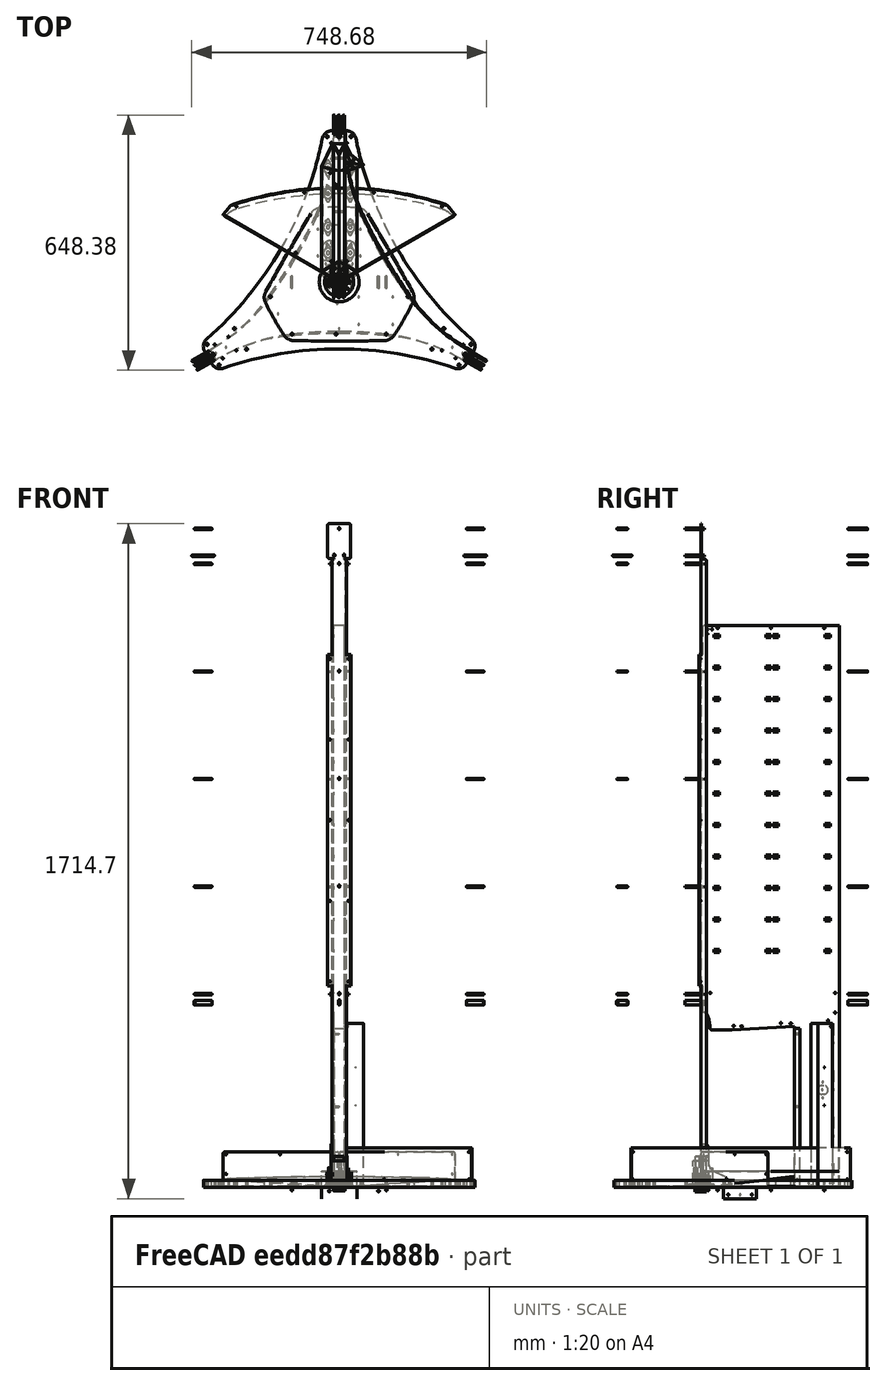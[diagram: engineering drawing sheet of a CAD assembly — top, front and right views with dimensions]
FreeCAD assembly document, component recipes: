
FREECAD ASSEMBLY — COMPONENT RECIPES ("composit_full_size3")

This assembly document has 76 components, labeled P0..P75 below (a component is one placed body or linked part). 73 of them carry a construction recipe — the FreeCAD feature program that regenerates the part from scratch, quoted from this document or its linked companion documents; the rest are supplied as boundary geometry only. No exploded tour is included for this assembly.
NOTE — document 2 of 3 of this assembly tour. The two overview renders and the header above are repeated from document 1; the component sections below continue where the previous document stopped.
COMPONENT P37 — recipe-attached ("hub2108", modeled in this document).
Construction recipe (the document's own serialized feature program — sketch geometry with constraints, then the solid features built on it; lengths are millimeters unless a unit is written):

FEATURE [PartDesign::SubShapeBinder] Binder
  BindCopyOnChange = 0
  BindMode = 0
  ClaimChildren = true
  Context = -> Body [Binder.]
  Fuse = false
  MakeFace = true
  OffsetFill = false
  OffsetIntersection = false
  OffsetJoinType = 0
  OffsetOpenResult = false
  PartialLoad = false
  Relative = true
  Support = -> [Compound001]
  _Version = 2
  expr: Support = <<part1_base>>._self
FEATURE [PartDesign::FeaturePython] BaseBend  # WARN: FeaturePython — macro-defined, semantics opaque (R4)
  BendSide = 1
  BendSketch = -> Binder
  MidPlane = false
  Reverse = false
  Suppressed = false
  length = 1428
  radius = 0.1
  thickness = 0.3
  expr: length = <<Properties>>.total_height
  expr: radius = composit_properties#<<Properties>>.bend_r
  expr: thickness = composit_properties#<<Properties>>.al_thickness
FEATURE [Sketcher::SketchObject] Sketch044
  ArcFitTolerance = 0
  AttachmentSupport = -> [YZ_Plane]
  ExternalGeometry = -> [Binder]
  FullyConstrained = false
  MakeInternals = false
  MapMode = 5
  Placement = pos=(0,0,0) rot=(0.57735,0.57735,0.57735;2.0944rad)
  expr: Constraints[16] = <<Properties>>.total_height
  expr: Constraints[23] = composit_properties#<<Properties>>.bend_r
  expr: Constraints[33] = <<Properties>>.petal_offset
  sketch-geometry (12):
    g0: LineSegment StartX=-41.6284 StartY=0 StartZ=0 EndX=4.96521 EndY=0 EndZ=0
    g1: LineSegment StartX=4.96521 StartY=0 StartZ=0 EndX=4.96521 EndY=512 EndZ=0
    g2: LineSegment StartX=4.96521 StartY=512 StartZ=0 EndX=-41.6284 EndY=512 EndZ=0
    g3: LineSegment StartX=-41.6284 StartY=512 StartZ=0 EndX=-41.6284 EndY=0 EndZ=0
    g4: LineSegment StartX=-41.6284 StartY=1428 StartZ=0 EndX=8.37158 EndY=1428 EndZ=0
    g5: LineSegment StartX=4.96521 StartY=1354 StartZ=0 EndX=-41.6284 EndY=1354 EndZ=0
    g6: LineSegment StartX=-41.6284 StartY=1354 StartZ=0 EndX=-41.6284 EndY=1428 EndZ=0
    g7: ArcOfCircle [constr] CenterX=4.96521 CenterY=0.1 CenterZ=0 NormalX=0 NormalY=0 NormalZ=1 AngleXU=0 Radius=0.1 StartAngle=3.66519 EndAngle=4.71239
    g8: LineSegment [constr] StartX=4.96521 StartY=0 StartZ=0 EndX=6.6679 EndY=0 EndZ=0
    g9: LineSegment [constr] StartX=4.87861 StartY=0.05 StartZ=0 EndX=2.02073 EndY=5 EndZ=0
    g10: LineSegment StartX=8.37158 StartY=1428 StartZ=0 EndX=4.96521 EndY=1424.59 EndZ=0
    g11: LineSegment StartX=4.96521 StartY=1424.59 StartZ=0 EndX=4.96521 EndY=1354 EndZ=0
  constraints (35):
    c: Coincident(g0,g1)
    c: Coincident(g1,g2)
    c: Coincident(g2,g3)
    c: Coincident(g3,g0)
    c: Horizontal(g0)
    c: Horizontal(g2)
    c: Vertical(g1)
    c: Vertical(g3)
    c: PointOnObject(g0,g-1)
    c: Coincident(g4,g10)
    c: Coincident(g11,g5)
    c: Coincident(g5,g6)
    c: Coincident(g6,g4)
    c: Horizontal(g4)
    c: Horizontal(g5)
    c: Vertical(g6)
    c: DistanceY(g4) = 1428
    c: DistanceY(g11,g10) = 74
    c: PointOnObject(g7,g-1)
    c: PointOnObject(g8,g-1)
    c: Tangent(g8,g7) = -1.5708
    c: Tangent(g9,g7) = 1.5708
    c: Angle(g9) = 2.0944
    c: Radius(g7) = 0.1
    c: PointOnObject(g-3,g9)
    c: DistanceY(g9) = 5
    c: PointOnObject(g7,g1)
    c: DistanceY(g1,g11) = 842
    c: Vertical(g2,g5)
    c: DistanceX(g4,g4) = 50
    c: Coincident(g10,g11)
    c: Vertical(g11)
    c: Angle(g10) = -2.35619
    c: DistanceX(g4) = 8.37158
    c: Vertical(g5,g1)
FEATURE [PartDesign::CoordinateSystem] Local_CS025  label="part1_bottom_LCS"
  AttacherType = Attacher::AttachEngine3D
  AttachmentSupport = -> [XY_Plane]
  MapMode = 5
FEATURE [PartDesign::CoordinateSystem] Local_CS026  label="part1_top_LCS"
  AttacherType = Attacher::AttachEngine3D
  AttachmentOffset = pos=(0,0,1428) rot=(0,0,1;0rad)
  AttachmentSupport = -> [XY_Plane]
  MapMode = 5
  Placement = pos=(0,0,1428) rot=(0,0,1;0rad)
  expr: .AttachmentOffset.Base.z = <<Properties>>.total_height
FEATURE [PartDesign::Boolean] Boolean001
  BaseFeature = -> BaseBend
  Group = -> [Compound016]
  Suppressed = false
  Type = 1
  UsePlacement = false
  expr: Group = <<part1_cut1>>._self
FEATURE [PartDesign::Boolean] Boolean002
  BaseFeature = -> Boolean001
  Group = -> [Compound026]
  Refine = true
  Suppressed = false
  Type = 0
  UsePlacement = false
  expr: Group = <<part1_fuse1>>._self
FEATURE [PartDesign::Pocket] Pocket025
  BaseFeature = -> Boolean002
  Direction = (-1,0,0)
  Length = 5
  Length2 = 5
  Midplane = true
  Profile = -> Sketch044
  ReferenceAxis = -> Sketch044 [N_Axis]
  Suppressed = false
  Type = 1
FEATURE [PartDesign::Boolean] Boolean005
  BaseFeature = -> Pocket025
  Group = -> [Compound024]
  Suppressed = false
  Type = 1
  UsePlacement = false
  expr: Group = <<part1_cut2>>._self
FEATURE [PartDesign::Body] Body  label="part1_material_0.30ansi"
  AllowCompound = false
  Group = -> [Binder,BaseBend,Boolean001,Boolean002,Sketch044,Pocket025,Boolean005,Local_CS025,Local_CS026]
  Origin = -> Origin
  Tip = -> Boolean005
COMPONENT P38 — same part as P37; its construction recipe is shown at P37.
COMPONENT P39 — same part as P37; its construction recipe is shown at P37.
COMPONENT P40 — recipe-attached ("top_top001", modeled in this document).
Construction recipe (the document's own serialized feature program — sketch geometry with constraints, then the solid features built on it; lengths are millimeters unless a unit is written):

FEATURE [Part::FeaturePython] Connect001  label="top_top_cut1_refined"  # WARN: FeaturePython — macro-defined, semantics opaque (R4)
  Objects = -> [Compound049]
  Refine = true
  Tolerance = 0
FEATURE [PartDesign::FeatureBase] BaseFeature
  BaseFeature = -> Hole003
  Suppressed = false
  expr: BaseFeature = <<Hole003>>._self
FEATURE [PartDesign::FeatureSubtractivePython] PDW_Sub  # link proxy (typed FeaturePython)
  BaseFeature = -> BaseFeature
  Body = Body110
  ClaimChildren = true
  EditPlacementAdjustments = false
  Enabled = 1
  LinkedObject = -> Connect001
  MeshTolerance = 0.1
  PatternBase = -> Connect001
  PatternBaseOffset = 0
  PatternBaseScale = 1
  PatternBaseScaleXYZ = (1,1,1)
  PatternOffsetCut = false
  PatternOffsetIntersection = false
  PatternOffsetJoin = 0
  PatternOffsetMode = 0
  PatternOffsetSelfIntersection = false
  PatternOperation = 0
  PatternOperationDefault = None
  PatternScaleCut = false
  PatternShapeOffset = 0
  PatternShapeScale = 1
  PatternShapeScaleXYZ = (1,1,1)
  PatternToolOffset = 0
  PatternToolScale = 1
  PatternToolScaleXYZ = (1,1,1)
  RefineMesh = true
  ShapeManagement = 0
  ShowMeshProps = false
  ShowOffsetProps = false
  ShowScaleProps = false
  ShowWarnings = true
  Suppressed = false
  TipBase = -> BaseFeature
  TipBaseOffset = 0
  TipBaseScale = 1
  TipBaseScaleXYZ = (1,1,1)
  TipOffsetCut = false
  TipOffsetIntersection = false
  TipOffsetJoin = 0
  TipOffsetMode = 0
  TipOffsetSelfIntersection = false
  TipOperation = 1
  TipOperationDefault = Cut
  TipScaleCut = false
  TipShapeOffset = 0
  TipShapeScale = 1
  TipShapeScaleXYZ = (1,1,1)
  TipTool = -> Connect001
  TipToolOffset = 0
  TipToolScale = 1
  TipToolScaleXYZ = (1,1,1)
  Type = Subtractive
  UsePatternBaseAddSubShape = false
  UsePatternToolAddSubShape = false
  UseTipBaseAddSubShape = false
  UseTipToolAddSubShape = false
  Version = 0.2023.08.13
FEATURE [PartDesign::Boolean] Boolean034
  BaseFeature = -> PDW_Sub
  Group = -> [Compound082]
  Suppressed = false
  Type = 1
  UsePlacement = false
FEATURE [PartDesign::CoordinateSystem] Local_CS031  label="dropper_fix_top_outer_LCS"
  AttacherType = Attacher::AttachEngine3D
  AttachmentSupport = -> [XY_Plane083]
  MapMode = 5
FEATURE [PartDesign::CoordinateSystem] Local_CS032  label="dropper_fix_top_inner_LCS"
  AttacherType = Attacher::AttachEngine3D
  AttachmentOffset = pos=(0,0,3) rot=(0,0,1;0rad)
  AttachmentSupport = -> [XY_Plane083]
  MapMode = 5
  Placement = pos=(0,0,3) rot=(0,0,1;0rad)
FEATURE [PartDesign::Body] Body110  label="dropper_fix_top"
  AllowCompound = false
  Group = -> [BaseFeature,PDW_Sub,Connect001,Boolean034,Local_CS031,Local_CS032]
  Origin = -> Origin083
  Tip = -> Boolean034
COMPONENT P41 — recipe-attached ("top_bottom001", modeled in this document).
Construction recipe (the document's own serialized feature program — sketch geometry with constraints, then the solid features built on it; lengths are millimeters unless a unit is written):

FEATURE [PartDesign::SubShapeBinder] Binder007
  BindCopyOnChange = 0
  BindMode = 0
  ClaimChildren = true
  Fuse = false
  MakeFace = true
  OffsetFill = false
  OffsetIntersection = false
  OffsetJoinType = 0
  OffsetOpenResult = false
  PartialLoad = false
  Relative = false
  Support = -> [Compound011]
  _Version = 2
FEATURE [PartDesign::Pad] Pad005
  Direction = (0,0,1)
  Length = 3
  Length2 = 10
  Profile = -> Binder007
  Suppressed = false
  Type = 0
FEATURE [Sketcher::SketchObject] Sketch025
  ArcFitTolerance = 0
  AttachmentSupport = -> [XY_Plane007]
  FullyConstrained = true
  MakeInternals = false
  MapMode = 5
FEATURE [PartDesign::SubShapeBinder] Binder021
  BindCopyOnChange = 0
  BindMode = 0
  ClaimChildren = true
  Fuse = false
  MakeFace = true
  OffsetFill = false
  OffsetIntersection = false
  OffsetJoinType = 0
  OffsetOpenResult = false
  PartialLoad = false
  Relative = false
  Support = -> [Compound014]
  _Version = 2
FEATURE [PartDesign::Pocket] Pocket006
  BaseFeature = -> Pad005
  Direction = (0,0,-1)
  Length = 5
  Length2 = 5
  Midplane = true
  Profile = -> Binder021
  Suppressed = false
  Type = 1
FEATURE [Sketcher::SketchObject] Sketch027
  ArcFitTolerance = 0
  AttachmentSupport = -> [XY_Plane007]
  FullyConstrained = true
  MakeInternals = false
  MapMode = 5
  sketch-geometry (1):
    g0: Circle CenterX=0 CenterY=40 CenterZ=0 NormalX=0 NormalY=0 NormalZ=1 AngleXU=0 Radius=4
  constraints (3):
    c: PointOnObject(g0,g-2)
    c: Diameter(g0) = 8
    c: DistanceY(g0) = 40
FEATURE [PartDesign::SubShapeBinder] Binder023
  BindCopyOnChange = 0
  BindMode = 0
  ClaimChildren = true
  Context = -> Body004 [Binder023.]
  Fuse = false
  MakeFace = true
  OffsetFill = false
  OffsetIntersection = false
  OffsetJoinType = 0
  OffsetOpenResult = false
  PartialLoad = false
  Relative = true
  Support = -> [Clone005]
  _Version = 2
FEATURE [Sketcher::SketchObject] Sketch028
  ArcFitTolerance = 0
  AttachmentSupport = -> [XY_Plane007]
  ExternalGeometry = -> [Binder023]
  FullyConstrained = true
  MakeInternals = false
  MapMode = 5
  expr: Constraints[9] = <<Properties>>.rivet_d
  sketch-geometry (10):
    g0: Circle CenterX=0 CenterY=59 CenterZ=0 NormalX=0 NormalY=0 NormalZ=1 AngleXU=0 Radius=1.7
    g1: Circle CenterX=0 CenterY=106.372 CenterZ=0 NormalX=0 NormalY=0 NormalZ=1 AngleXU=0 Radius=1.7
    g2: Circle CenterX=0 CenterY=181.372 CenterZ=0 NormalX=0 NormalY=0 NormalZ=1 AngleXU=0 Radius=1.7
    g3: Circle CenterX=0 CenterY=256.372 CenterZ=0 NormalX=0 NormalY=0 NormalZ=1 AngleXU=0 Radius=1.7
    g4: Circle CenterX=0 CenterY=303.743 CenterZ=0 NormalX=0 NormalY=0 NormalZ=1 AngleXU=0 Radius=1.7
    g5: LineSegment [constr] StartX=28.3 StartY=73.8716 StartZ=0 EndX=28.3 EndY=106.372 EndZ=0
    g6: LineSegment [constr] StartX=28.3 StartY=106.372 StartZ=0 EndX=28.3 EndY=138.872 EndZ=0
    g7: LineSegment [constr] StartX=28.3 StartY=138.872 StartZ=0 EndX=28.3 EndY=181.372 EndZ=0
    g8: LineSegment [constr] StartX=28.3 StartY=181.372 StartZ=0 EndX=28.3 EndY=223.872 EndZ=0
    g9: LineSegment [constr] StartX=28.3 StartY=223.872 StartZ=0 EndX=28.3 EndY=256.372 EndZ=0
  constraints (24):
    c: PointOnObject(g0,g-2)
    c: PointOnObject(g1,g-2)
    c: PointOnObject(g2,g-2)
    c: PointOnObject(g3,g-2)
    c: DistanceY(g0) = 59
    c: Equal(g0, g1-g4) x4
    c: Diameter(g0) = 3.4
    c: Coincident(g5,g-3)
    c: Vertical(g5)
    c: Coincident(g5,g6)
    c: Coincident(g6,g-4)
    c: Coincident(g6,g7)
    c: Vertical(g7)
    c: Coincident(g7,g8)
    c: Coincident(g8,g-5)
    c: Coincident(g8,g9)
    c: Vertical(g9)
    c: Equal(g5,g6)
    c: Equal(g6,g9)
    c: Equal(g7,g8)
    c: Horizontal(g2,g7)
    c: Horizontal(g1,g5)
    c: Horizontal(g3,g9)
    c: Symmetric(g0,g4,g2)
FEATURE [PartDesign::Hole] Hole003
  BaseFeature = -> Pocket006
  CustomThreadClearance = 0
  Depth = 25
  DepthType = 0
  Diameter = 3.4
  DrillForDepth = false
  DrillPoint = 1
  DrillPointAngle = 118
  HoleCutCountersinkAngle = 90
  HoleCutCustomValues = false
  HoleCutDepth = 0
  HoleCutDiameter = 6.1
  HoleCutType = 0
  ModelThread = false
  Profile = -> Sketch028
  Reversed = true
  Suppressed = false
  Tapered = false
  TaperedAngle = 90
  ThreadClass = 0
  ThreadDepth = 25
  ThreadDepthType = 0
  ThreadDirection = 0
  ThreadFit = 0
  ThreadSize = 0
  ThreadType = 0
  Threaded = false
  UseCustomThreadClearance = false
  expr: Diameter = <<Properties>>.rivet_d
FEATURE [Part::Compound] Compound048  label="top_bottom_cut1"
  Links = -> [Extrude016,Extrude017]
FEATURE [Part::FeaturePython] Connect  label="top_bottom_cut1_refined"  # WARN: FeaturePython — macro-defined, semantics opaque (R4)
  Objects = -> [Compound048]
  Refine = true
  Tolerance = 0
FEATURE [PartDesign::Boolean] Boolean033
  BaseFeature = -> Hole003
  Group = -> [Compound081]
  Suppressed = false
  Type = 1
  UsePlacement = false
FEATURE [PartDesign::FeatureSubtractivePython] PDW_Common_Sub  # link proxy (typed FeaturePython)
  BaseFeature = -> Boolean033
  Body = Body004
  ClaimChildren = true
  EditPlacementAdjustments = false
  Enabled = 1
  LinkedObject = -> Connect
  MeshTolerance = 0.1
  PatternBaseOffset = 0
  PatternBaseScale = 1
  PatternBaseScaleXYZ = (1,1,1)
  PatternOffsetCut = false
  PatternOffsetIntersection = false
  PatternOffsetJoin = 0
  PatternOffsetMode = 0
  PatternOffsetSelfIntersection = false
  PatternOperation = 3
  PatternOperationDefault = Common
  PatternScaleCut = false
  PatternShapeOffset = 0
  PatternShapeScale = 1
  PatternShapeScaleXYZ = (1,1,1)
  PatternTool = -> Compound048
  PatternToolOffset = 0
  PatternToolScale = 1
  PatternToolScaleXYZ = (1,1,1)
  Refine = true
  RefineMesh = true
  ShapeManagement = 1
  ShowMeshProps = false
  ShowOffsetProps = false
  ShowScaleProps = false
  ShowWarnings = true
  Suppressed = false
  TipBase = -> Boolean033
  TipBaseOffset = 0
  TipBaseScale = 1
  TipBaseScaleXYZ = (1,1,1)
  TipOffsetCut = false
  TipOffsetIntersection = false
  TipOffsetJoin = 0
  TipOffsetMode = 0
  TipOffsetSelfIntersection = false
  TipOperation = 1
  TipOperationDefault = Common
  TipScaleCut = false
  TipShapeOffset = 0
  TipShapeScale = 1
  TipShapeScaleXYZ = (1,1,1)
  TipTool = -> Connect
  TipToolOffset = 0
  TipToolScale = 1
  TipToolScaleXYZ = (1,1,1)
  Type = Subtractive
  UsePatternBaseAddSubShape = false
  UsePatternToolAddSubShape = false
  UseTipBaseAddSubShape = true
  UseTipToolAddSubShape = true
  Version = 0.2023.08.13
FEATURE [PartDesign::CoordinateSystem] Local_CS029  label="dropper_fix_bottom_outer_LCS"
  AttacherType = Attacher::AttachEngine3D
  AttachmentSupport = -> [XY_Plane007]
  MapMode = 5
FEATURE [PartDesign::CoordinateSystem] Local_CS030  label="dropper_fix_bottom_inner_LCS"
  AttacherType = Attacher::AttachEngine3D
  AttachmentOffset = pos=(0,0,3) rot=(0,0,1;0rad)
  AttachmentSupport = -> [XY_Plane007]
  MapMode = 5
  Placement = pos=(0,0,3) rot=(0,0,1;0rad)
FEATURE [PartDesign::Body] Body004  label="dropper_fix_bottom"
  AllowCompound = false
  Group = -> [Binder007,Pad005,Sketch025,Binder021,Pocket006,Sketch027,Sketch028,Binder023,Hole003,Boolean033,PDW_Common_Sub,Compound048,Connect,Local_CS029,Local_CS030]
  Origin = -> Origin007
  Tip = -> PDW_Common_Sub
COMPONENT P42 — recipe-attached ("cap_outer_material_0.30ansi001", modeled in this document).
Construction recipe (the document's own serialized feature program — sketch geometry with constraints, then the solid features built on it; lengths are millimeters unless a unit is written):

FEATURE [PartDesign::SubShapeBinder] Binder012
  BindCopyOnChange = 0
  BindMode = 0
  ClaimChildren = true
  Fuse = false
  MakeFace = true
  OffsetFill = false
  OffsetIntersection = false
  OffsetJoinType = 0
  OffsetOpenResult = false
  PartialLoad = false
  Placement = pos=(0,0,40) rot=(0,0,1;0rad)
  Relative = false
  Support = -> [Compound012]
  _Version = 2
FEATURE [PartDesign::SubShapeBinder] Binder013
  BindCopyOnChange = 0
  BindMode = 0
  ClaimChildren = true
  Fuse = false
  MakeFace = true
  OffsetFill = false
  OffsetIntersection = false
  OffsetJoinType = 0
  OffsetOpenResult = false
  PartialLoad = false
  Placement = pos=(0,0,40) rot=(0,0,1;0rad)
  Relative = false
  Support = -> [Compound013]
  _Version = 2
FEATURE [PartDesign::FeaturePython] BaseBend007  # WARN: FeaturePython — macro-defined, semantics opaque (R4)
  BendSide = 1
  BendSketch = -> Binder012
  MidPlane = false
  Reverse = true
  Suppressed = false
  length = 100
  radius = 0.1
  thickness = 0.3
  expr: radius = composit_properties#<<Properties>>.bend_r
  expr: thickness = composit_properties#<<Properties>>.al_thickness
FEATURE [PartDesign::FeaturePython] Bend001  # WARN: FeaturePython — macro-defined, semantics opaque (R4)
  AutoMiter = false
  BaseFeature = -> BaseBend007
  BendType = 0
  LengthList = [47]
  LengthSpec = 1
  NonperforationMaxLength = 5
  Perforate = false
  PerforationAngle = 0
  PerforationInitialLength = 5
  PerforationMaxLength = 5
  ReliefFactor = 0.7
  Suppressed = false
  UseReliefFactor = false
  angle = 90
  baseObject = -> BaseBend007 [Edge14,Edge30,Edge46,Edge62,Edge70,Edge86,Edge102,Edge116]
  bendAList = [90]
  extend1 = 0
  extend2 = 0
  gap1 = 0
  gap2 = 0
  invert = false
  kfactor = 0.5
  length = 47
  maxExtendDist = 5
  minGap = 0.1
  minReliefGap = 1
  miterangle1 = 0
  miterangle2 = 0
  offset = 0
  radius = 0.1
  reliefType = 0
  reliefd = 1
  reliefw = 0.8
  sketchflip = false
  sketchinvert = false
  unfold = false
  expr: radius = BaseBend007.radius
FEATURE [PartDesign::Pocket] Pocket002
  BaseFeature = -> Bend001
  Direction = (0,0,-1)
  Length = 5
  Length2 = 5
  Profile = -> Binder013 [Face1]
  Refine = true
  Reversed = true
  Suppressed = false
  Type = 1
FEATURE [PartDesign::SubShapeBinder] Binder014
  BindCopyOnChange = 0
  BindMode = 0
  ClaimChildren = true
  Context = -> Link012 [Binder014.]
  Fuse = false
  MakeFace = true
  OffsetFill = false
  OffsetIntersection = false
  OffsetJoinType = 0
  OffsetOpenResult = false
  PartialLoad = false
  Relative = true
  Support = -> [Sketch019]
  _Version = 2
FEATURE [Sketcher::SketchObject] Sketch020
  ArcFitTolerance = 0
  AttachmentSupport = -> [XY_Plane005]
  FullyConstrained = true
  MakeInternals = false
  MapMode = 5
  expr: Constraints[10] = composit_properties#<<Properties>>.bend_r + composit_properties#<<Properties>>.al_thickness
  sketch-geometry (5):
    g0: ArcOfCircle CenterX=0 CenterY=0.46188 CenterZ=0 NormalX=0 NormalY=0 NormalZ=1 AngleXU=0 Radius=5 StartAngle=0.523599 EndAngle=2.61799
    g1: LineSegment StartX=0 StartY=0 StartZ=0 EndX=4.53013 EndY=2.61547 EndZ=0
    g2: LineSegment StartX=4.53013 StartY=2.61547 StartZ=0 EndX=4.33013 EndY=2.96188 EndZ=0
    g3: LineSegment StartX=0 StartY=0 StartZ=0 EndX=-4.53013 EndY=2.61547 EndZ=0
    g4: LineSegment StartX=-4.53013 StartY=2.61547 StartZ=0 EndX=-4.33013 EndY=2.96188 EndZ=0
  constraints (13):
    c: PointOnObject(g0,g-2)
    c: Coincident(g1,g-1)
    c: Coincident(g2,g1)
    c: Coincident(g3,g1)
    c: Coincident(g4,g3)
    c: Perpendicular(g3,g4)
    c: Perpendicular(g1,g2)
    c: Tangent(g2,g0) = -1.5708
    c: Tangent(g4,g0) = 1.5708
    c: Equal(g4,g2)
    c: Distance(g2) = 0.4
    c: Diameter(g0) = 10
    c: Angle(g1,g3) = 2.0944
FEATURE [PartDesign::SubShapeBinder] Binder015
  BindCopyOnChange = 0
  BindMode = 0
  ClaimChildren = false
  Context = -> Link012 [Binder015.]
  Fuse = false
  MakeFace = true
  OffsetFill = false
  OffsetIntersection = false
  OffsetJoinType = 0
  OffsetOpenResult = false
  PartialLoad = false
  Relative = true
  Support = -> [Sketch002]
  _Version = 2
  expr: Support = <<dropper_fix_sketch>>._self
FEATURE [Sketcher::SketchObject] Sketch022  label="cap_outer_shape"
  ArcFitTolerance = 0
  AttachmentSupport = -> [YZ_Plane005]
  ExternalGeometry = -> [Binder012]
  FullyConstrained = true
  MakeInternals = false
  MapMode = 5
  Placement = pos=(0,0,0) rot=(0.57735,0.57735,0.57735;2.0944rad)
  expr: Constraints[11] = composit_properties#<<Properties>>.bend_r + composit_properties#<<Properties>>.al_thickness
  expr: Constraints[9] = composit_properties#<<Properties>>.bend_r + composit_properties#<<Properties>>.al_thickness + 0.01 mm
  sketch-geometry (5):
    g0: LineSegment StartX=351.882 StartY=40.41 StartZ=0 EndX=0 EndY=40.41 EndZ=0
    g1: LineSegment StartX=0 StartY=40.41 StartZ=0 EndX=0 EndY=0 EndZ=0
    g2: LineSegment StartX=0 StartY=0 StartZ=0 EndX=351.882 EndY=0 EndZ=0
    g3: LineSegment StartX=351.882 StartY=0 StartZ=0 EndX=351.882 EndY=40.41 EndZ=0
    g4: GeomPoint [constr] X=351.872 Y=40.4 Z=0
  constraints (14):
    c: Coincident(g0,g1)
    c: Coincident(g1,g2)
    c: Coincident(g2,g3)
    c: Coincident(g3,g0)
    c: Horizontal(g0)
    c: Horizontal(g2)
    c: Vertical(g1)
    c: Vertical(g3)
    c: Coincident(g1,g-1)
    c: DistanceY(g-3,g0) = 0.41
    c: DistanceX(g-3,g0) = 0.01
    c: DistanceY(g-3,g4) = 0.4
    c: Vertical(g-3,g4)
    c: DistanceY(g4) = 40.4  'height'
FEATURE [Part::FeaturePython] WireFilter002  # WARN: FeaturePython — macro-defined, semantics opaque (R4)
  AttacherType = Attacher::AttachEngine3D
  ClaimChildren = true
  ColorKeyCount = 8
  Colorize = true
  FaceMaker = 5
  FixNormal = false
  FollowSource = true
  InvertedFaceScale = 5
  MaxWires = 25
  Normal = (1,0,0)
  OffsetFill = false
  OffsetIntersection = false
  OffsetJoin = 0
  OffsetOpenResult = false
  Scale = (1,1,1)
  SelectEdges = false
  Source = -> Sketch022
  UniformScale = 1
  UseDefault = false
  UseSelected = true
  UseSelectedEdges = false
  Version = 0.2022.02.09
  WireOrder = [1]
FEATURE [PartDesign::SubShapeBinder] Binder132
  BindCopyOnChange = 0
  BindMode = 0
  ClaimChildren = true
  Fuse = false
  MakeFace = true
  OffsetFill = false
  OffsetIntersection = false
  OffsetJoinType = 0
  OffsetOpenResult = false
  PartialLoad = false
  Relative = false
  Support = -> [Sketch017]
  _Version = 2
FEATURE [PartDesign::Pocket] Pocket125
  BaseFeature = -> Pocket002
  Direction = (0,0,-1)
  Length = 5
  Length2 = 5
  Midplane = true
  Profile = -> Binder014
  Suppressed = false
  Type = 1
FEATURE [PartDesign::Pocket] Pocket003
  BaseFeature = -> Pocket125
  Direction = (0,0,-1)
  Length = 5
  Length2 = 5
  Midplane = true
  Profile = -> Sketch020
  ReferenceAxis = -> Sketch020 [N_Axis]
  Suppressed = false
  Type = 1
FEATURE [PartDesign::Mirrored] Mirrored
  BaseFeature = -> Pocket003
  MirrorPlane = -> YZ_Plane005
  Suppressed = false
  TransformMode = 0
FEATURE [PartDesign::Pocket] Pocket005
  BaseFeature = -> Mirrored
  Direction = (-1,0,0)
  Length = 5
  Length2 = 5
  Midplane = true
  Profile = -> WireFilter002
  Suppressed = false
  Type = 1
FEATURE [PartDesign::Boolean] Boolean032
  BaseFeature = -> Pocket005
  Group = -> [Compound080]
  Suppressed = false
  Type = 1
  UsePlacement = false
FEATURE [PartDesign::Body] Body002  label="cap_outer_material_0.30ansi"
  AllowCompound = false
  Group = -> [Binder012,Binder013,BaseBend007,Bend001,Pocket002,Binder014,Sketch020,Pocket125,Pocket003,Binder015,Mirrored,Sketch022,WireFilter002,Pocket005,Binder132,Boolean032]
  Origin = -> Origin005
  Tip = -> Boolean032
COMPONENT P43 — recipe-attached ("cap_inner2_material_0.30ansi001", modeled in this document).
Construction recipe (the document's own serialized feature program — sketch geometry with constraints, then the solid features built on it; lengths are millimeters unless a unit is written):

FEATURE [PartDesign::SubShapeBinder] Binder018
  BindCopyOnChange = 0
  BindMode = 0
  ClaimChildren = false
  Fuse = false
  MakeFace = true
  OffsetFill = false
  OffsetIntersection = false
  OffsetJoinType = 0
  OffsetOpenResult = false
  PartialLoad = false
  Relative = false
  Support = -> [Body002[BaseBend007.Binder012.Compound012.Part__Mirroring006.Sketch016.]]
  _Version = 2
FEATURE [PartDesign::SubShapeBinder] Binder019
  BindCopyOnChange = 0
  BindMode = 0
  ClaimChildren = false
  Fuse = false
  MakeFace = false
  OffsetFill = false
  OffsetIntersection = false
  OffsetJoinType = 0
  OffsetOpenResult = false
  PartialLoad = false
  Relative = false
  Support = -> [Sketch019]
  _Version = 2
FEATURE [Sketcher::SketchObject] Sketch024
  ArcFitTolerance = 0
  AttachmentSupport = -> [XY_Plane023]
  ExternalGeometry = -> [Binder019,Binder018]
  FullyConstrained = true
  MakeInternals = false
  MapMode = 5
  expr: Constraints[10] = composit_properties#<<Properties>>.thickness + composit_properties#<<Properties>>.al_thickness + composit_properties#<<Properties>>.bend_r
  sketch-geometry (5):
    g0: LineSegment StartX=-41.7 StartY=272.288 StartZ=0 EndX=-41.7 EndY=289.736 EndZ=0
    g1: LineSegment StartX=-41.7 StartY=289.736 StartZ=0 EndX=41.7 EndY=289.736 EndZ=0
    g2: LineSegment StartX=41.7 StartY=289.736 StartZ=0 EndX=41.7 EndY=272.288 EndZ=0
    g3: LineSegment StartX=41.7 StartY=272.288 StartZ=0 EndX=-41.7 EndY=272.288 EndZ=0
    g4: GeomPoint [constr] X=0 Y=281.012 Z=0
  constraints (13):
    c: Coincident(g0,g1)
    c: Coincident(g1,g2)
    c: Coincident(g2,g3)
    c: Coincident(g3,g0)
    c: Horizontal(g1)
    c: Horizontal(g3)
    c: Vertical(g0)
    c: Vertical(g2)
    c: Symmetric(g1,g0,g4)
    c: PointOnObject(g4,g-2)
    c: DistanceX(g1,g-4) = 3.4
    c: DistanceY(g2,g-3) = 5
    c: DistanceY(g1,g-4) = 3
FEATURE [PartDesign::FeaturePython] BaseBend008  # WARN: FeaturePython — macro-defined, semantics opaque (R4)
  BendSide = 0
  BendSketch = -> Sketch024
  MidPlane = false
  Reverse = false
  Suppressed = false
  length = 100
  radius = 0.1
  thickness = 0.3
  expr: radius = composit_properties#<<Properties>>.bend_r
  expr: thickness = composit_properties#<<Properties>>.al_thickness
FEATURE [Sketcher::SketchObject] Sketch217
  ArcFitTolerance = 0
  AttachmentSupport = -> [XY_Plane023]
  ExternalGeometry = -> [Sketch024,Binder018]
  FullyConstrained = true
  MakeInternals = false
  MapMode = 5
  sketch-geometry (6):
    g0: LineSegment StartX=41.7 StartY=289.736 StartZ=0 EndX=14.25 EndY=348.472 EndZ=0
    g1: LineSegment StartX=0 StartY=348.472 StartZ=0 EndX=14.25 EndY=348.472 EndZ=0
    g2: LineSegment [constr] StartX=14.25 StartY=351.872 StartZ=0 EndX=14.25 EndY=348.472 EndZ=0
    g3: LineSegment [constr] StartX=14.25 StartY=348.472 StartZ=0 EndX=17.3302 EndY=349.911 EndZ=0
    g4: LineSegment StartX=0 StartY=348.472 StartZ=0 EndX=0 EndY=289.736 EndZ=0
    g5: LineSegment StartX=0 StartY=289.736 StartZ=0 EndX=41.7 EndY=289.736 EndZ=0
  constraints (17):
    c: Coincident(g0,g-3)
    c: PointOnObject(g1,g-2)
    c: Coincident(g1,g0)
    c: Horizontal(g1)
    c: Coincident(g2,g0)
    c: Coincident(g2,g3)
    c: PointOnObject(g3,g-4)
    c: Perpendicular(g0,g3)
    c: Perpendicular(g1,g2)
    c: Equal(g3,g2)
    c: DistanceY(g2,g2) = 3.4
    c: Horizontal(g2,g-4)
    c: Coincident(g4,g1)
    c: PointOnObject(g4,g-3)
    c: Vertical(g4)
    c: Coincident(g5,g4)
    c: Coincident(g5,g0)
FEATURE [PartDesign::Pad] Pad033
  BaseFeature = -> BaseBend008
  Direction = (0,0,1)
  Length = 0.3
  Length2 = 10
  Profile = -> Sketch217
  ReferenceAxis = -> Sketch217 [N_Axis]
  Suppressed = false
  Type = 0
FEATURE [PartDesign::Mirrored] Mirrored016
  BaseFeature = -> Pad033
  MirrorPlane = -> Sketch217 [V_Axis]
  Originals = -> [Pad033]
  Suppressed = false
  TransformMode = 0
FEATURE [PartDesign::Hole] Hole002
  BaseFeature = -> Mirrored016
  CustomThreadClearance = 0
  Depth = 25
  DepthType = 0
  Diameter = 3.4
  DrillForDepth = false
  DrillPoint = 1
  DrillPointAngle = 118
  HoleCutCountersinkAngle = 90
  HoleCutCustomValues = false
  HoleCutDepth = 0
  HoleCutDiameter = 6.1
  HoleCutType = 0
  ModelThread = false
  Profile = -> Binder019
  Refine = true
  Reversed = true
  Suppressed = false
  Tapered = false
  TaperedAngle = 90
  ThreadClass = 0
  ThreadDepth = 25
  ThreadDepthType = 0
  ThreadDirection = 0
  ThreadFit = 0
  ThreadSize = 0
  ThreadType = 0
  Threaded = false
  UseCustomThreadClearance = false
  expr: Diameter = <<Properties>>.rivet_d
FEATURE [PartDesign::Body] Body016  label="cap_inner2_material_0.30ansi"
  AllowCompound = false
  Group = -> [Binder018,Binder019,Sketch024,BaseBend008,Sketch217,Pad033,Mirrored016,Hole002]
  Origin = -> Origin023
  Tip = -> Hole002
COMPONENT P44 — recipe-attached ("top_connector_material_0.30ansi001", modeled in this document).
Construction recipe (the document's own serialized feature program — sketch geometry with constraints, then the solid features built on it; lengths are millimeters unless a unit is written):

FEATURE [Sketcher::SketchObject] Sketch029  label="top_connector_base_sketch"
  ArcFitTolerance = 0
  AttachmentOffset = pos=(0,0,-35) rot=(0,0,1;0rad)
  AttachmentSupport = -> [XZ_Plane024]
  FullyConstrained = true
  MakeInternals = false
  MapMode = 5
  Placement = pos=(0,35,-7.8e-15) rot=(1,0,0;1.5708rad)
  expr: .Constraints.width = <<Properties>>.inner_width
  sketch-geometry (5):
    g0: LineSegment StartX=-11.5 StartY=-13 StartZ=0 EndX=-11.5 EndY=-1.95e-14 EndZ=0
    g1: LineSegment StartX=-11.5 StartY=-1.95e-14 StartZ=0 EndX=11.5 EndY=-1.95e-14 EndZ=0
    g2: LineSegment StartX=11.5 StartY=-1.95e-14 StartZ=0 EndX=11.5 EndY=-13 EndZ=0
    g3: LineSegment [constr] StartX=11.5 StartY=-13 StartZ=0 EndX=-11.5 EndY=-13 EndZ=0
    g4: GeomPoint [constr] X=-3.6e-15 Y=-6.5 Z=0
  constraints (13):
    c: Coincident(g0,g1)
    c: Coincident(g1,g2)
    c: Coincident(g2,g3)
    c: Coincident(g3,g0)
    c: Horizontal(g1)
    c: Horizontal(g3)
    c: Vertical(g0)
    c: Vertical(g2)
    c: Symmetric(g1,g0,g4)
    c: PointOnObject(g4,g-2)
    c: PointOnObject(g1,g-1)
    c: DistanceX(g1,g1) = 23  'width'
    c: DistanceY(g2,g2) = 13  'height'
FEATURE [PartDesign::FeaturePython] BaseBend009  # WARN: FeaturePython — macro-defined, semantics opaque (R4)
  BendSide = 0
  BendSketch = -> Sketch029
  MidPlane = false
  Reverse = true
  Suppressed = false
  length = 283.743
  radius = 0.1
  thickness = 0.3
  expr: radius = composit_properties#<<Properties>>.bend_r
  expr: thickness = composit_properties#<<Properties>>.al_thickness
FEATURE [PartDesign::SubShapeBinder] Binder029
  BindCopyOnChange = 0
  BindMode = 0
  ClaimChildren = false
  Context = -> Body017 [Binder029.]
  Fuse = false
  MakeFace = true
  OffsetFill = false
  OffsetIntersection = false
  OffsetJoinType = 0
  OffsetOpenResult = false
  PartialLoad = false
  Relative = true
  Support = -> [Sketch027]
  _Version = 2
  expr: Support = Sketch027._self
FEATURE [PartDesign::SubShapeBinder] Binder030
  BindCopyOnChange = 0
  BindMode = 0
  ClaimChildren = false
  Context = -> Body017 [Binder030.]
  Fuse = false
  MakeFace = true
  OffsetFill = false
  OffsetIntersection = false
  OffsetJoinType = 0
  OffsetOpenResult = false
  PartialLoad = false
  Relative = true
  Support = -> [Sketch028]
  _Version = 2
  expr: Support = Sketch028._self
FEATURE [PartDesign::Hole] Hole004
  BaseFeature = -> BaseBend009
  CustomThreadClearance = 0
  Depth = 25
  DepthType = 0
  Diameter = 3.4
  DrillForDepth = false
  DrillPoint = 1
  DrillPointAngle = 118
  HoleCutCountersinkAngle = 90
  HoleCutCustomValues = false
  HoleCutDepth = 0
  HoleCutDiameter = 6.1
  HoleCutType = 0
  ModelThread = false
  Profile = -> Binder030
  Suppressed = false
  Tapered = false
  TaperedAngle = 90
  ThreadClass = 0
  ThreadDepth = 25
  ThreadDepthType = 0
  ThreadDirection = 0
  ThreadFit = 0
  ThreadSize = 0
  ThreadType = 0
  Threaded = false
  UseCustomThreadClearance = false
  expr: Diameter = <<Properties>>.rivet_d
FEATURE [Sketcher::SketchObject] Sketch048
  ArcFitTolerance = 0
  AttachmentSupport = -> [YZ_Plane024]
  FullyConstrained = true
  MakeInternals = false
  MapMode = 5
  Placement = pos=(0,0,0) rot=(0.57735,0.57735,0.57735;2.0944rad)
  expr: Constraints[5] = -<<top_connector_base_sketch>>.Constraints.height
  expr: Constraints[7] = -<<top_connector_base_sketch>>.AttachmentOffset.Base.z
  sketch-geometry (3):
    g0: ArcOfCircle CenterX=42 CenterY=-6 CenterZ=0 NormalX=0 NormalY=0 NormalZ=1 AngleXU=0 Radius=7 StartAngle=3.14159 EndAngle=4.71239
    g1: LineSegment StartX=42 StartY=-13 StartZ=0 EndX=35 EndY=-13 EndZ=0
    g2: LineSegment StartX=35 StartY=-6 StartZ=0 EndX=35 EndY=-13 EndZ=0
  constraints (8):
    c: Horizontal(g1)
    c: Coincident(g2,g1)
    c: Vertical(g2)
    c: Tangent(g1,g0) = 1.5708
    c: Tangent(g2,g0) = -1.5708
    c: DistanceY(g1) = -13
    c: DistanceY(g0) = -6
    c: DistanceX(g1) = 35
FEATURE [PartDesign::Boolean] Boolean007
  BaseFeature = -> Hole004
  Group = -> [Compound078]
  Suppressed = false
  Type = 1
  UsePlacement = false
  expr: Group = <<top_connector_cut1>>._self
FEATURE [PartDesign::Pocket] Pocket027
  BaseFeature = -> Boolean007
  Direction = (-1,0,0)
  Length = 5
  Length2 = 5
  Midplane = true
  Profile = -> Sketch048
  ReferenceAxis = -> Sketch048 [N_Axis]
  Suppressed = false
  Type = 1
FEATURE [PartDesign::Body] Body017  label="top_connector_material_0.30ansi"
  AllowCompound = false
  Group = -> [Sketch029,BaseBend009,Binder029,Binder030,Hole004,Boolean007,Sketch048,Pocket027]
  Origin = -> Origin024
  Tip = -> Pocket027
COMPONENT P45 — recipe-attached ("cap_inner1_material_0.30ansi001", modeled in this document).
Construction recipe (the document's own serialized feature program — sketch geometry with constraints, then the solid features built on it; lengths are millimeters unless a unit is written):

FEATURE [PartDesign::SubShapeBinder] Binder016
  BindCopyOnChange = 0
  BindMode = 0
  ClaimChildren = true
  Fuse = false
  MakeFace = false
  OffsetFill = false
  OffsetIntersection = false
  OffsetJoinType = 0
  OffsetOpenResult = false
  PartialLoad = false
  Relative = false
  Support = -> [Sketch019]
  _Version = 2
FEATURE [PartDesign::SubShapeBinder] Binder020
  BindCopyOnChange = 0
  BindMode = 0
  ClaimChildren = false
  Context = -> Link015 [Binder020.]
  Fuse = false
  MakeFace = true
  OffsetFill = false
  OffsetIntersection = false
  OffsetJoinType = 0
  OffsetOpenResult = false
  PartialLoad = false
  Relative = true
  Support = -> [Body002[BaseBend007.Binder012.Compound012.Part__Mirroring006.Sketch016.]]
  _Version = 2
FEATURE [Sketcher::SketchObject] Sketch023
  ArcFitTolerance = 0
  AttachmentSupport = -> [XY_Plane006]
  ExternalGeometry = -> [Binder020]
  FullyConstrained = true
  MakeInternals = false
  MapMode = 5
  expr: Constraints[9] = composit_properties#<<Properties>>.thickness + composit_properties#<<Properties>>.bend_r + composit_properties#<<Properties>>.al_thickness
  sketch-geometry (5):
    g0: LineSegment StartX=41.7 StartY=29.0385 StartZ=0 EndX=-41.7 EndY=29.0385 EndZ=0
    g1: LineSegment StartX=-41.7 StartY=29.0385 StartZ=0 EndX=-41.7 EndY=58.0385 EndZ=0
    g2: LineSegment StartX=-41.7 StartY=58.0385 StartZ=0 EndX=41.7 EndY=58.0385 EndZ=0
    g3: LineSegment StartX=41.7 StartY=58.0385 StartZ=0 EndX=41.7 EndY=29.0385 EndZ=0
    g4: GeomPoint [constr] X=0 Y=43.5385 Z=0
  constraints (13):
    c: Coincident(g0,g1)
    c: Coincident(g1,g2)
    c: Coincident(g2,g3)
    c: Coincident(g3,g0)
    c: Horizontal(g0)
    c: Horizontal(g2)
    c: Vertical(g1)
    c: Vertical(g3)
    c: DistanceY(g-3,g0) = 3
    c: DistanceX(g0,g-3) = 3.4
    c: PointOnObject(g4,g-2)
    c: Symmetric(g2,g0,g4)
    c: DistanceY(g3,g3) = 29
FEATURE [PartDesign::Pad] Pad007
  Direction = (0,0,1)
  Length = 0.3
  Length2 = 10
  Profile = -> Sketch023
  ReferenceAxis = -> Sketch023 [N_Axis]
  Suppressed = false
  Type = 0
  expr: Length = composit_properties#<<Properties>>.al_thickness
FEATURE [PartDesign::FeaturePython] Bend002  label="cap_inner1_bend"  # WARN: FeaturePython — macro-defined, semantics opaque (R4)
  AutoMiter = true
  BaseFeature = -> Pad007
  BendType = 0
  LengthList = [31]
  LengthSpec = 0
  NonperforationMaxLength = 5
  Perforate = false
  PerforationAngle = 0
  PerforationInitialLength = 5
  PerforationMaxLength = 5
  ReliefFactor = 0.7
  Suppressed = false
  UseReliefFactor = false
  angle = 90
  baseObject = -> Pad007 [Edge12,Edge7]
  bendAList = [90]
  extend1 = 0
  extend2 = 0
  gap1 = 0
  gap2 = 0
  invert = false
  kfactor = 0.5
  length = 31
  maxExtendDist = 5
  minGap = 0.1
  minReliefGap = 1
  miterangle1 = 0
  miterangle2 = 0
  offset = 0
  radius = 0.1
  reliefType = 0
  reliefd = 1
  reliefw = 0.8
  sketchflip = false
  sketchinvert = false
  unfold = false
  expr: length = <<cap_outer_shape>>.Constraints.height - composit_properties#<<Properties>>.thickness - composit_properties#<<Properties>>.al_thickness - composit_properties#<<Properties>>.bend_r - 6 mm
  expr: radius = BaseBend007.radius
FEATURE [PartDesign::Hole] Hole001
  BaseFeature = -> Bend002
  CustomThreadClearance = 0
  Depth = 25
  DepthType = 0
  Diameter = 3.4
  DrillForDepth = false
  DrillPoint = 1
  DrillPointAngle = 118
  HoleCutCountersinkAngle = 90
  HoleCutCustomValues = false
  HoleCutDepth = 0
  HoleCutDiameter = 6.1
  HoleCutType = 0
  ModelThread = false
  Profile = -> Binder016
  Reversed = true
  Suppressed = false
  Tapered = false
  TaperedAngle = 90
  ThreadClass = 0
  ThreadDepth = 25
  ThreadDepthType = 0
  ThreadDirection = 0
  ThreadFit = 0
  ThreadSize = 0
  ThreadType = 0
  Threaded = false
  UseCustomThreadClearance = false
  expr: Diameter = <<Properties>>.rivet_d
FEATURE [PartDesign::Body] Body003  label="cap_inner1_material_0.30ansi"
  AllowCompound = false
  Group = -> [Sketch023,Binder016,Binder020,Pad007,Bend002,Hole001]
  Origin = -> Origin006
  Tip = -> Hole001
COMPONENT P46 — same part as P37; its construction recipe is shown at P37.
COMPONENT P47 — recipe-attached ("part2_material_0.30ansi001", modeled in this document).
Construction recipe (the document's own serialized feature program — sketch geometry with constraints, then the solid features built on it; lengths are millimeters unless a unit is written):

FEATURE [PartDesign::SubShapeBinder] Binder001
  BindCopyOnChange = 0
  BindMode = 0
  ClaimChildren = true
  Context = -> Body001 [Binder001.]
  Fuse = false
  MakeFace = true
  OffsetFill = false
  OffsetIntersection = false
  OffsetJoinType = 0
  OffsetOpenResult = false
  PartialLoad = false
  Placement = pos=(0,0,0) rot=(0,0,1;4.18879rad)
  Relative = false
  Support = -> [Array001]
  _Version = 2
  expr: Support = <<2part_base>>._self
FEATURE [PartDesign::FeaturePython] BaseBend001  # WARN: FeaturePython — macro-defined, semantics opaque (R4)
  BendSide = 0
  BendSketch = -> Binder001
  MidPlane = false
  Reverse = false
  Suppressed = false
  length = 1428
  radius = 0.1
  thickness = 0.3
  expr: length = <<Properties>>.total_height
  expr: radius = composit_properties#<<Properties>>.bend_r
  expr: thickness = composit_properties#<<Properties>>.al_thickness
FEATURE [PartDesign::CoordinateSystem] Local_CS027  label="part2_bottom"
  AttacherType = Attacher::AttachEngine3D
  AttachmentOffset = pos=(0,0,0) rot=(0,0,1;2.0944rad)
  AttachmentSupport = -> [XY_Plane001]
  MapMode = 5
  Placement = pos=(0,0,0) rot=(0,0,1;2.0944rad)
FEATURE [PartDesign::CoordinateSystem] Local_CS028
  AttacherType = Attacher::AttachEngine3D
  AttachmentOffset = pos=(0,0,1428) rot=(0,0,1;0rad)
  AttachmentSupport = -> [Local_CS027]
  MapMode = 5
  Placement = pos=(0,0,1428) rot=(0,0,1;2.0944rad)
  expr: .AttachmentOffset.Base.z = <<Properties>>.total_height
FEATURE [PartDesign::Boolean] Boolean
  BaseFeature = -> BaseBend001
  Group = -> [Compound021]
  Refine = true
  Suppressed = false
  Type = 1
  UsePlacement = false
  expr: Group = <<part2_cut1>>._self
FEATURE [PartDesign::Boolean] Boolean003
  BaseFeature = -> Boolean
  Group = -> [Compound007]
  Refine = true
  Suppressed = false
  Type = 0
  UsePlacement = false
  expr: Group = <<part2_fuse1>>._self
FEATURE [PartDesign::Boolean] Boolean006
  BaseFeature = -> Boolean003
  Group = -> [Compound025]
  Suppressed = false
  Type = 1
  UsePlacement = false
  expr: Group = <<part2_cut2>>._self
FEATURE [PartDesign::Body] Body001  label="part2_material_0.30ansi"
  AllowCompound = false
  Group = -> [Binder001,BaseBend001,Boolean,Boolean003,Boolean006,Local_CS027,Local_CS028]
  Origin = -> Origin001
  Tip = -> Boolean006
COMPONENT P48 — recipe-attached ("bot_hor_amplifier_material_0.30ansi001", modeled in this document).
Construction recipe (the document's own serialized feature program — sketch geometry with constraints, then the solid features built on it; lengths are millimeters unless a unit is written):

FEATURE [Sketcher::SketchObject] Sketch049
  ArcFitTolerance = 0
  AttachmentSupport = -> [YZ_Plane030]
  FullyConstrained = true
  MakeInternals = false
  MapMode = 5
  Placement = pos=(0,0,0) rot=(0.57735,0.57735,0.57735;2.0944rad)
  expr: Constraints[11] = <<Properties>>.inner_width
  sketch-geometry (5):
    g0: LineSegment StartX=-11.5 StartY=-14 StartZ=0 EndX=-11.5 EndY=0 EndZ=0
    g1: LineSegment StartX=-11.5 StartY=0 StartZ=0 EndX=11.5 EndY=0 EndZ=0
    g2: LineSegment StartX=11.5 StartY=0 StartZ=0 EndX=11.5 EndY=-14 EndZ=0
    g3: LineSegment [constr] StartX=11.5 StartY=-14 StartZ=0 EndX=-11.5 EndY=-14 EndZ=0
    g4: GeomPoint [constr] X=0 Y=-7 Z=0
  constraints (13):
    c: Coincident(g0,g1)
    c: Coincident(g1,g2)
    c: Coincident(g2,g3)
    c: Coincident(g3,g0)
    c: Horizontal(g1)
    c: Horizontal(g3)
    c: Vertical(g0)
    c: Vertical(g2)
    c: Symmetric(g1,g0,g4)
    c: PointOnObject(g4,g-2)
    c: PointOnObject(g1,g-1)
    c: DistanceX(g1,g1) = 23
    c: DistanceY(g2) = -14
FEATURE [PartDesign::FeaturePython] BaseBend019  # WARN: FeaturePython — macro-defined, semantics opaque (R4)
  BendSide = 0
  BendSketch = -> Sketch049
  MidPlane = true
  Reverse = false
  Suppressed = false
  length = 250
  radius = 0.1
  thickness = 0.3
FEATURE [PartDesign::Boolean] Boolean009
  BaseFeature = -> BaseBend019
  Group = -> [Fusion008]
  Suppressed = false
  Type = 1
  UsePlacement = false
FEATURE [PartDesign::Body] Body068  label="bot_hor_amplifier_material_0.30ansi"
  AllowCompound = false
  Group = -> [BaseBend019,Sketch049,Boolean009]
  Origin = -> Origin030
  Tip = -> Boolean009
COMPONENT P49 — recipe-attached ("star_material_0.30ansi001", modeled in this document).
Construction recipe (the document's own serialized feature program — sketch geometry with constraints, then the solid features built on it; lengths are millimeters unless a unit is written):

FEATURE [Sketcher::SketchObject] Sketch032
  ArcFitTolerance = 0
  AttachmentSupport = -> [XZ_Plane025]
  FullyConstrained = true
  MakeInternals = false
  MapMode = 5
  Placement = pos=(0,0,0) rot=(1,0,0;1.5708rad)
  expr: Constraints[11] = <<Properties>>.inner_width
  sketch-geometry (5):
    g0: LineSegment StartX=-11.5 StartY=-12 StartZ=0 EndX=-11.5 EndY=-2.84e-14 EndZ=0
    g1: LineSegment StartX=-11.5 StartY=-2.84e-14 StartZ=0 EndX=11.5 EndY=-2.84e-14 EndZ=0
    g2: LineSegment StartX=11.5 StartY=-2.84e-14 StartZ=0 EndX=11.5 EndY=-12 EndZ=0
    g3: LineSegment [constr] StartX=11.5 StartY=-12 StartZ=0 EndX=-11.5 EndY=-12 EndZ=0
    g4: GeomPoint [constr] X=-5.1e-15 Y=-6 Z=0
  constraints (13):
    c: Coincident(g0,g1)
    c: Coincident(g1,g2)
    c: Coincident(g2,g3)
    c: Coincident(g3,g0)
    c: Horizontal(g1)
    c: Horizontal(g3)
    c: Vertical(g0)
    c: Vertical(g2)
    c: Symmetric(g1,g0,g4)
    c: PointOnObject(g4,g-2)
    c: PointOnObject(g1,g-1)
    c: DistanceX(g1,g1) = 23
    c: DistanceY(g2,g2) = 12
FEATURE [PartDesign::FeaturePython] BaseBend010  # WARN: FeaturePython — macro-defined, semantics opaque (R4)
  BendSide = 0
  BendSketch = -> Sketch032
  MidPlane = false
  Reverse = true
  Suppressed = false
  length = 35
  radius = 0.1
  thickness = 0.3
  expr: radius = composit_properties#<<Properties>>.bend_r
  expr: thickness = composit_properties#<<Properties>>.al_thickness
FEATURE [Sketcher::SketchObject] Sketch033
  ArcFitTolerance = 0
  AttachmentSupport = -> [XY_Plane025]
  FullyConstrained = true
  MakeInternals = false
  MapMode = 5
  expr: Constraints[6] = composit_properties#<<Properties>>.bend_r + composit_properties#<<Properties>>.al_thickness
  expr: Constraints[7] = <<Properties>>.inner_width / 2
  sketch-geometry (7):
    g0: LineSegment StartX=0 StartY=-1.289e-13 StartZ=0 EndX=11.1 EndY=6.40859 EndZ=0
    g1: LineSegment StartX=11.5 StartY=0 StartZ=0 EndX=0 EndY=-1.289e-13 EndZ=0
    g2: LineSegment StartX=11.1 StartY=6.40859 StartZ=0 EndX=11.1 EndY=8.33953 EndZ=0
    g3: LineSegment StartX=11.1 StartY=8.33953 StartZ=0 EndX=11.5 EndY=8.33953 EndZ=0
    g4: GeomPoint [constr] X=11.5 Y=6.63953 Z=0
    g5: LineSegment StartX=11.5 StartY=8.33953 StartZ=0 EndX=11.5 EndY=6.63953 EndZ=0
    g6: LineSegment StartX=11.5 StartY=6.63953 StartZ=0 EndX=11.5 EndY=0 EndZ=0
  constraints (18):
    c: Coincident(g-1,g0)
    c: Coincident(g0,g2)
    c: Coincident(g3,g5)
    c: PointOnObject(g6,g-1)
    c: Coincident(g6,g1)
    c: Coincident(g1,g0)
    c: DistanceX(g2,g3) = 0.4
    c: DistanceX(g1,g1) = 11.5
    c: Coincident(g2,g3)
    c: Horizontal(g3)
    c: Vertical(g2)
    c: PointOnObject(g4,g0)
    c: DistanceY(g4,g5) = 1.7
    c: Angle(g0) = 0.523599
    c: Coincident(g5,g6)
    c: Vertical(g5)
    c: Vertical(g6)
    c: Coincident(g5,g4)
FEATURE [PartDesign::Pocket] Pocket018
  BaseFeature = -> BaseBend010
  Direction = (0,0,-1)
  Length = 5
  Length2 = 5
  Profile = -> Sketch033
  ReferenceAxis = -> Sketch033 [N_Axis]
  Suppressed = false
  Type = 1
FEATURE [PartDesign::Mirrored] Mirrored001
  BaseFeature = -> Pocket018
  MirrorPlane = -> Sketch033 [V_Axis]
  Originals = -> [Pocket018]
  Suppressed = false
  TransformMode = 0
FEATURE [Sketcher::SketchObject] Sketch034
  ArcFitTolerance = 0
  AttachmentSupport = -> [YZ_Plane025]
  ExternalGeometry = -> [Sketch033]
  FullyConstrained = false
  MakeInternals = false
  MapMode = 5
  Placement = pos=(0,0,0) rot=(0.57735,0.57735,0.57735;2.0944rad)
  sketch-geometry (4):
    g0: LineSegment StartX=6.63953 StartY=-25.0734 StartZ=0 EndX=22.8156 EndY=-25.0734 EndZ=0
    g1: LineSegment StartX=22.8156 StartY=-25.0734 StartZ=0 EndX=8.57047 EndY=-0.4 EndZ=0
    g2: LineSegment StartX=6.63953 StartY=-0.4 StartZ=0 EndX=6.63953 EndY=-25.0734 EndZ=0
    g3: LineSegment StartX=6.63953 StartY=-0.4 StartZ=0 EndX=8.57047 EndY=-0.4 EndZ=0
  constraints (11):
    c: Coincident(g2,g0)
    c: Horizontal(g0)
    c: Coincident(g0,g1)
    c: Vertical(g2)
    c: Coincident(g3,g2)
    c: Coincident(g3,g1)
    c: Horizontal(g3)
    c: Angle(g1) = 2.0944
    c: DistanceY(g2) = -0.4
    c: PointOnObject(g-3,g2)
    c: PointOnObject(g-3,g1)
FEATURE [PartDesign::Pocket] Pocket019
  BaseFeature = -> Mirrored001
  Direction = (-1,0,0)
  Length = 5
  Length2 = 5
  Midplane = true
  Profile = -> Sketch034
  ReferenceAxis = -> Sketch034 [N_Axis]
  Suppressed = false
  Type = 1
FEATURE [Sketcher::SketchObject] Sketch036
  ArcFitTolerance = 0
  AttachmentSupport = -> [XY_Plane025]
  FullyConstrained = true
  MakeInternals = false
  MapMode = 5
  sketch-geometry (1):
    g0: Circle CenterX=0 CenterY=25 CenterZ=0 NormalX=0 NormalY=0 NormalZ=1 AngleXU=0 Radius=3
  constraints (3):
    c: PointOnObject(g0,g-2)
    c: DistanceY(g0) = 25
    c: Diameter(g0) = 6
FEATURE [PartDesign::Pocket] Pocket021
  BaseFeature = -> Pocket019
  Direction = (0,0,-1)
  Length = 5
  Length2 = 5
  Profile = -> Sketch036
  ReferenceAxis = -> Sketch036 [N_Axis]
  Suppressed = false
  Type = 0
FEATURE [Sketcher::SketchObject] Sketch045
  ArcFitTolerance = 0
  AttachmentSupport = -> [YZ_Plane025]
  FullyConstrained = true
  MakeInternals = false
  MapMode = 5
  Placement = pos=(0,0,0) rot=(0.57735,0.57735,0.57735;2.0944rad)
  expr: Constraints[0] = <<BaseBend010>>.length
  sketch-geometry (5):
    g0: ArcOfCircle CenterX=30 CenterY=-7 CenterZ=0 NormalX=0 NormalY=0 NormalZ=1 AngleXU=0 Radius=5 StartAngle=4.71239 EndAngle=6.28319
    g1: LineSegment StartX=35 StartY=-7 StartZ=0 EndX=35 EndY=-25 EndZ=0
    g2: LineSegment StartX=30 StartY=-12 StartZ=0 EndX=0 EndY=-12 EndZ=0
    g3: LineSegment StartX=35 StartY=-25 StartZ=0 EndX=0 EndY=-25 EndZ=0
    g4: LineSegment StartX=0 StartY=-25 StartZ=0 EndX=0 EndY=-12 EndZ=0
  constraints (14):
    c: DistanceX(g0) = 35
    c: Vertical(g1)
    c: Tangent(g1,g0) = 1.5708
    c: PointOnObject(g2,g-2)
    c: Horizontal(g2)
    c: Coincident(g3,g1)
    c: PointOnObject(g3,g-2)
    c: Horizontal(g3)
    c: Coincident(g4,g3)
    c: Coincident(g4,g2)
    c: Tangent(g2,g0) = 1.5708
    c: DistanceY(g0) = -7
    c: DistanceY(g3) = -25
    c: Radius(g0) = 5
FEATURE [PartDesign::Pocket] Pocket026
  BaseFeature = -> Pocket021
  Direction = (-1,0,0)
  Length = 5
  Length2 = 5
  Midplane = true
  Profile = -> Sketch045
  ReferenceAxis = -> Sketch045 [N_Axis]
  Suppressed = false
  Type = 1
FEATURE [PartDesign::Boolean] Boolean004
  BaseFeature = -> Pocket026
  Group = -> [Compound077]
  Suppressed = false
  Type = 1
  UsePlacement = false
  expr: Group = <<star_amplifier_cut1>>._self
FEATURE [PartDesign::FeatureAdditivePython] PDW_Common_Add002  # link proxy (typed FeaturePython)
  BaseFeature = -> Boolean004
  Body = Body018
  ClaimChildren = false
  EditPlacementAdjustments = false
  Enabled = 1
  LinkedObject = -> Boolean004
  MeshTolerance = 0.1
  PatternBase = -> Pocket026
  PatternBaseOffset = 0
  PatternBaseScale = 1
  PatternBaseScaleXYZ = (1,1,1)
  PatternOffsetCut = false
  PatternOffsetIntersection = false
  PatternOffsetJoin = 0
  PatternOffsetMode = 0
  PatternOffsetSelfIntersection = false
  PatternOperation = 3
  PatternOperationDefault = Common
  PatternScaleCut = false
  PatternShapeOffset = 0
  PatternShapeScale = 1
  PatternShapeScaleXYZ = (1,1,1)
  PatternTool = -> Boolean004
  PatternToolOffset = 0
  PatternToolScale = 1
  PatternToolScaleXYZ = (1,1,1)
  RefineMesh = true
  ShapeManagement = 0
  ShowMeshProps = false
  ShowOffsetProps = false
  ShowScaleProps = false
  ShowWarnings = true
  Suppressed = false
  TipBase = -> Pocket026
  TipBaseOffset = 0
  TipBaseScale = 1
  TipBaseScaleXYZ = (1,1,1)
  TipOffsetCut = false
  TipOffsetIntersection = false
  TipOffsetJoin = 0
  TipOffsetMode = 0
  TipOffsetSelfIntersection = false
  TipOperation = 2
  TipOperationDefault = Common
  TipScaleCut = false
  TipShapeOffset = 0
  TipShapeScale = 1
  TipShapeScaleXYZ = (1,1,1)
  TipTool = -> Boolean004
  TipToolOffset = 0
  TipToolScale = 1
  TipToolScaleXYZ = (1,1,1)
  Type = Additive
  UsePatternBaseAddSubShape = false
  UsePatternToolAddSubShape = true
  UseTipBaseAddSubShape = false
  UseTipToolAddSubShape = true
  Version = 0.2023.08.13
FEATURE [PartDesign::PolarPattern] PolarPattern008
  Angle = 360
  Axis = -> Z_Axis025
  BaseFeature = -> PDW_Common_Add002
  Mode = 0
  Occurrences = 3
  Offset = 120
  Originals = -> [PDW_Common_Add002]
  Refine = true
  Suppressed = false
  TransformMode = 0
FEATURE [PartDesign::Body] Body018  label="star_material_0.30ansi"
  AllowCompound = false
  Group = -> [Sketch032,BaseBend010,Sketch033,Pocket018,Mirrored001,Sketch034,Pocket019,Sketch036,Pocket021,Sketch045,Pocket026,Boolean004,PDW_Common_Add002,PolarPattern008]
  Origin = -> Origin025
  Placement = pos=(0,0,1428) rot=(0,0,1;0rad)
  Tip = -> PolarPattern008
  expr: .Placement.Base.z = <<Properties>>.total_height
COMPONENT P50 — recipe-attached ("plexiglass_outer_material_0.30ansi001", modeled in this document).
Construction recipe (the document's own serialized feature program — sketch geometry with constraints, then the solid features built on it; lengths are millimeters unless a unit is written):

FEATURE [PartDesign::SubShapeBinder] Binder037
  BindCopyOnChange = 0
  BindMode = 0
  ClaimChildren = true
  Context = -> Body072 [Binder037.]
  Fuse = false
  MakeFace = true
  OffsetFill = false
  OffsetIntersection = false
  OffsetJoinType = 0
  OffsetOpenResult = false
  PartialLoad = false
  Relative = false
  Support = -> [Compound036]
  _Version = 2
FEATURE [PartDesign::FeaturePython] BaseBend018  # WARN: FeaturePython — macro-defined, semantics opaque (R4)
  BendSide = 1
  BendSketch = -> Binder037
  MidPlane = false
  Placement = pos=(0,0,1596) rot=(0,0,1;0rad)
  Reverse = true
  Suppressed = false
  length = 1203
  radius = 1
  thickness = 1.5
FEATURE [PartDesign::FeaturePython] Extend  # WARN: FeaturePython — macro-defined, semantics opaque (R4)
  BaseFeature = -> BaseBend018
  Offset = 0.02
  Refine = true
  Suppressed = false
  UseSubtraction = false
  baseObject = -> BaseBend018 [Face32]
  gap1 = 0
  gap2 = 0
  length = 0
FEATURE [PartDesign::Boolean] Boolean013
  BaseFeature = -> Extend
  Group = -> [Populate018]
  Suppressed = false
  Type = 1
  UsePlacement = false
FEATURE [PartDesign::Body] Body072  label="plexiglass_outer_material_0.30ansi"
  AllowCompound = false
  Group = -> [Binder037,BaseBend018,Extend,Boolean013]
  Origin = -> Origin035
  Tip = -> Extend
COMPONENT P51 — recipe-attached ("pillar_bottom_material_0.30ansi001", modeled in this document).
Construction recipe (the document's own serialized feature program — sketch geometry with constraints, then the solid features built on it; lengths are millimeters unless a unit is written):

FEATURE [Sketcher::SketchObject] Sketch011  label="pillar_bottom_cut_vert"
  ArcFitTolerance = 0
  AttachmentSupport = -> [XZ_Plane015]
  FullyConstrained = true
  MakeInternals = false
  MapMode = 5
  Placement = pos=(0,0,0) rot=(1,0,0;1.5708rad)
  expr: Constraints[15] = <<pillar_bottom_BaseBend>>.length
  expr: Constraints[16] = <<pillar_bottom_BaseBend>>.radius + <<pillar_bottom_BaseBend>>.thickness
  expr: Constraints[27] = <<pillar_base_sketch>>.Constraints.length - 4 mm
  sketch-geometry (15):
    g0: LineSegment StartX=-50.5 StartY=0 StartZ=0 EndX=-50.5 EndY=75 EndZ=0
    g1: LineSegment StartX=-45.5 StartY=80 StartZ=0 EndX=-40.5 EndY=80 EndZ=0
    g2: LineSegment StartX=50.5 StartY=4 StartZ=0 EndX=50.5 EndY=0 EndZ=0
    g3: LineSegment StartX=50.5 StartY=0 StartZ=0 EndX=-50.5 EndY=0 EndZ=0
    g4: ArcOfCircle CenterX=-45.5 CenterY=75 CenterZ=0 NormalX=0 NormalY=0 NormalZ=1 AngleXU=0 Radius=5 StartAngle=1.5708 EndAngle=3.14159
    g5: GeomPoint [constr] X=-50.5 Y=80 Z=0
    g6: ArcOfCircle CenterX=-40.5 CenterY=75 CenterZ=0 NormalX=0 NormalY=0 NormalZ=1 AngleXU=0 Radius=5 StartAngle=-9e-16 EndAngle=1.5708
    g7: GeomPoint [constr] X=-35.5 Y=80 Z=0
    g8: ArcOfCircle CenterX=45.5 CenterY=4 CenterZ=0 NormalX=0 NormalY=0 NormalZ=1 AngleXU=0 Radius=5 StartAngle=0 EndAngle=1.13485
    g9: GeomPoint [constr] X=50.5 Y=7.18672 Z=0
    g10: LineSegment StartX=-35.5 StartY=75 StartZ=0 EndX=-35.5 EndY=64.709 EndZ=0
    g11: LineSegment StartX=-19.6724 StartY=39.8753 StartZ=0 EndX=47.6113 EndY=8.53236 EndZ=0
    g12: ArcOfCircle CenterX=-8.10401 CenterY=64.709 CenterZ=0 NormalX=0 NormalY=0 NormalZ=1 AngleXU=0 Radius=27.396 StartAngle=3.14159 EndAngle=4.27645
    g13: GeomPoint [constr] X=-19.6724 Y=39.8753 Z=0
    g14: GeomPoint [constr] X=-13.5 Y=37 Z=0
  constraints (34):
    c: PointOnObject(g0,g-1)
    c: Vertical(g0)
    c: Horizontal(g1)
    c: Vertical(g2)
    c: Coincident(g2,g3)
    c: Coincident(g3,g0)
    c: PointOnObject(g5,g0)
    c: PointOnObject(g5,g1)
    c: Tangent(g0,g4) = 1.5708
    c: Tangent(g1,g4) = 1.5708
    c: PointOnObject(g7,g1)
    c: Tangent(g1,g6) = 1.5708
    c: PointOnObject(g9,g2)
    c: Tangent(g2,g8) = 1.5708
    c: Symmetric(g0,g2,g-2)
    c: DistanceX(g3,g3) = 101
    c: DistanceY(g2) = 4
    c: DistanceY(g5) = 80  'height'
    c: Radius(g4) = 5
    c: Radius(g8) = 5
    c: Equal(g4,g6)
    c: PointOnObject(g7,g10)
    c: PointOnObject(g9,g11)
    c: Vertical(g10)
    c: Tangent(g10,g6) = 1.5708
    c: Tangent(g12,g10) = -1.5708
    c: Tangent(g12,g11) = -1.5708
    c: DistanceX(g5,g7) = 15
    c: Tangent(g11,g8) = 1.5708
    c: Coincident(g11,g13)
    c: PointOnObject(g14,g11)
    c: DistanceY(g14) = 37
    c: DistanceX(g0,g14) = 37
    c: DistanceX(g11) = -19.6724
FEATURE [Sketcher::SketchObject] Sketch012
  ArcFitTolerance = 0
  AttachmentSupport = -> [XY_Plane015]
  FullyConstrained = true
  MakeInternals = false
  MapMode = 5
  expr: Constraints[18] = <<pillar_bottom_BaseSketch>>.Constraints.leg_length
  expr: Constraints[20] = <<pillar_bottom_BaseBend>>.radius + <<pillar_bottom_BaseBend>>.thickness
  expr: Constraints[9] = <<pillar_bottom_BaseBend>>.length
  sketch-geometry (9):
    g0: LineSegment StartX=-50.5 StartY=-4 StartZ=0 EndX=-50.5 EndY=0 EndZ=0
    g1: LineSegment StartX=-50.5 StartY=0 StartZ=0 EndX=50.5 EndY=0 EndZ=0
    g2: LineSegment StartX=50.5 StartY=0 StartZ=0 EndX=50.5 EndY=-4 EndZ=0
    g3: LineSegment StartX=29.5 StartY=-25 StartZ=0 EndX=-29.5 EndY=-25 EndZ=0
    g4: GeomPoint [constr] X=0 Y=-12.5 Z=0
    g5: ArcOfCircle CenterX=29.5 CenterY=-4 CenterZ=0 NormalX=0 NormalY=0 NormalZ=1 AngleXU=0 Radius=21 StartAngle=4.71239 EndAngle=6.28319
    g6: GeomPoint [constr] X=50.5 Y=-25 Z=0
    g7: ArcOfCircle CenterX=-29.5 CenterY=-4 CenterZ=0 NormalX=0 NormalY=0 NormalZ=1 AngleXU=0 Radius=21 StartAngle=3.14159 EndAngle=4.71239
    g8: GeomPoint [constr] X=-50.5 Y=-25 Z=0
  constraints (21):
    c: Coincident(g0,g1)
    c: Coincident(g1,g2)
    c: Horizontal(g1)
    c: Horizontal(g3)
    c: Vertical(g0)
    c: Vertical(g2)
    c: Symmetric(g1,g8,g4)
    c: PointOnObject(g4,g-2)
    c: PointOnObject(g1,g-1)
    c: DistanceX(g1,g1) = 101
    c: PointOnObject(g6,g2)
    c: PointOnObject(g6,g3)
    c: Tangent(g2,g5) = 1.5708
    c: Tangent(g3,g5) = 1.5708
    c: PointOnObject(g8,g0)
    c: PointOnObject(g8,g3)
    c: Tangent(g0,g7) = 1.5708
    c: Tangent(g3,g7) = 1.5708
    c: DistanceY(g6,g-1) = 25
    c: Equal(g7,g5)
    c: DistanceY(g2,g-1) = 4
FEATURE [Part::FeaturePython] WireFilter  # WARN: FeaturePython — macro-defined, semantics opaque (R4)
  AttacherType = Attacher::AttachEngine3D
  ClaimChildren = true
  ColorKeyCount = 8
  Colorize = true
  FaceMaker = 5
  FixNormal = false
  FollowSource = true
  InvertedFaceScale = 20
  MaxWires = 25
  Normal = (0,1,-2e-16)
  OffsetFill = false
  OffsetIntersection = false
  OffsetJoin = 0
  OffsetOpenResult = false
  Scale = (1,1,1)
  SelectEdges = false
  Source = -> Sketch011
  UniformScale = 1
  UseDefault = false
  UseSelected = true
  UseSelectedEdges = false
  Version = 0.2022.02.09
  WireOrder = [1]
FEATURE [Part::FeaturePython] WireFilter001  # WARN: FeaturePython — macro-defined, semantics opaque (R4)
  AttacherType = Attacher::AttachEngine3D
  ClaimChildren = true
  ColorKeyCount = 8
  Colorize = true
  FaceMaker = 5
  FixNormal = false
  FollowSource = true
  InvertedFaceScale = 5
  MaxWires = 25
  Normal = (0,0,1)
  OffsetFill = false
  OffsetIntersection = false
  OffsetJoin = 0
  OffsetOpenResult = false
  Scale = (1,1,1)
  SelectEdges = false
  Source = -> Sketch012
  UniformScale = 1
  UseDefault = false
  UseSelected = true
  UseSelectedEdges = false
  Version = 0.2022.02.09
  WireOrder = [1]
FEATURE [Sketcher::SketchObject] Sketch070
  ArcFitTolerance = 0
  AttachmentSupport = -> [XY_Plane015]
  FullyConstrained = true
  MakeInternals = false
  MapMode = 5
  sketch-geometry (2):
    g0: Circle CenterX=-40 CenterY=-12 CenterZ=0 NormalX=0 NormalY=0 NormalZ=1 AngleXU=0 Radius=2.75
    g1: Circle CenterX=40 CenterY=-12 CenterZ=0 NormalX=0 NormalY=0 NormalZ=1 AngleXU=0 Radius=2.75
  constraints (5):
    c: Equal(g1,g0)
    c: Diameter(g1) = 5.5
    c: Symmetric(g0,g1,g-2)
    c: DistanceX(g0,g1) = 80
    c: DistanceY(g1) = -12
FEATURE [Sketcher::SketchObject] Sketch118
  ArcFitTolerance = 0
  AttachmentSupport = -> [XZ_Plane015]
  FullyConstrained = true
  MakeInternals = false
  MapMode = 5
  Placement = pos=(0,0,0) rot=(1,0,0;1.5708rad)
  expr: Constraints[10] = <<pillar_base_sketch>>.Constraints.length / 2 - 2 mm
  expr: Constraints[9] = -<<pillar_bottom_BaseBend>>.length / 2
  sketch-geometry (11):
    g0: Circle CenterX=-43 CenterY=9 CenterZ=0 NormalX=0 NormalY=0 NormalZ=1 AngleXU=0 Radius=1.7
    g1: Circle CenterX=-43 CenterY=40.3333 CenterZ=0 NormalX=0 NormalY=0 NormalZ=1 AngleXU=0 Radius=1.7
    g2: Circle [constr] CenterX=-43 CenterY=103 CenterZ=0 NormalX=0 NormalY=0 NormalZ=1 AngleXU=0 Radius=1.7
    g3: LineSegment [constr] StartX=-43 StartY=9 StartZ=0 EndX=-43 EndY=40.3333 EndZ=0
    g4: GeomPoint [constr] X=-50.5 Y=0 Z=0
    g5: GeomPoint [constr] X=-43 Y=110 Z=0
    g6: LineSegment [constr] StartX=-43 StartY=103 StartZ=0 EndX=-43 EndY=110 EndZ=0
    g7: LineSegment [constr] StartX=-43 StartY=9 StartZ=0 EndX=-43 EndY=0 EndZ=0
    g8: LineSegment [constr] StartX=-43 StartY=40.3333 StartZ=0 EndX=-43 EndY=71.6667 EndZ=0
    g9: LineSegment [constr] StartX=-43 StartY=71.6667 StartZ=0 EndX=-43 EndY=103 EndZ=0
    g10: Circle CenterX=-43 CenterY=71.6667 CenterZ=0 NormalX=0 NormalY=0 NormalZ=1 AngleXU=0 Radius=1.7
  constraints (27):
    c: Equal(g0,g1)
    c: Equal(g0,g2)
    c: Diameter(g0) = 3.4
    c: Coincident(g3,g0)
    c: Coincident(g3,g1)
    c: Vertical(g3)
    c: Coincident(g8,g1)
    c: Coincident(g9,g2)
    c: PointOnObject(g4,g-1)
    c: DistanceX(g4) = -50.5
    c: DistanceX(g4,g0) = 7.5
    c: DistanceY(g5) = 110
    c: Coincident(g6,g2)
    c: Coincident(g6,g5)
    c: Vertical(g6)
    c: Coincident(g7,g0)
    c: PointOnObject(g7,g-1)
    c: Vertical(g7)
    c: DistanceY(g7,g7) = 9
    c: DistanceY(g6,g6) = 7
    c: Coincident(g8,g9)
    c: Vertical(g8)
    c: Vertical(g9)
    c: Equal(g3,g8)
    c: Equal(g8,g9)
    c: Coincident(g10,g8)
    c: Equal(g0,g10)
FEATURE [PartDesign::CoordinateSystem] pillar_bottom_LCS
  AttacherType = Attacher::AttachEngine3D
  AttachmentOffset = pos=(-50.5,0,0) rot=(0,0,1;0rad)
  AttachmentSupport = -> [XY_Plane015]
  MapMode = 5
  Placement = pos=(-50.5,0,0) rot=(0,0,1;0rad)
FEATURE [Sketcher::SketchObject] Sketch289  label="pillar_bottom_BaseSketch"
  ArcFitTolerance = 0
  AttacherType = Attacher::AttachEngine3D
  AttachmentSupport = -> [XY_Plane015]
  FullyConstrained = true
  MakeInternals = false
  MapMode = 5
  sketch-geometry (2):
    g0: LineSegment StartX=0 StartY=110 StartZ=0 EndX=0 EndY=0 EndZ=0
    g1: LineSegment StartX=0 StartY=0 StartZ=0 EndX=-25 EndY=0 EndZ=0
  constraints (7):
    c: PointOnObject(g0,g-2)
    c: Vertical(g0)
    c: Coincident(g0,g1)
    c: PointOnObject(g1,g-1)
    c: Horizontal(g1)
    c: DistanceX(g1,g1) = 25  'leg_length'
    c: DistanceY(g0,g0) = 110  'height'
FEATURE [PartDesign::FeaturePython] BaseBend060  label="pillar_bottom_BaseBend"  # WARN: FeaturePython — macro-defined, semantics opaque (R4)
  BendSide = 0
  BendSketch = -> Sketch289
  MidPlane = true
  Placement = pos=(0,0,0) rot=(0.57735,0.57735,0.57735;2.0944rad)
  Reverse = false
  Suppressed = false
  length = 101
  radius = 2
  thickness = 2
FEATURE [PartDesign::Pocket] Pocket
  BaseFeature = -> BaseBend060
  Direction = (0,-1,2e-16)
  Length = 5
  Length2 = 5
  Placement = pos=(0,0,0) rot=(0.57735,0.57735,0.57735;2.0944rad)
  Profile = -> WireFilter
  Suppressed = false
  Type = 1
FEATURE [PartDesign::Pocket] Pocket001
  BaseFeature = -> Pocket
  Direction = (0,0,-1)
  Length = 5
  Length2 = 5
  Placement = pos=(0,0,0) rot=(0.57735,0.57735,0.57735;2.0944rad)
  Profile = -> WireFilter001
  Reversed = true
  Suppressed = false
  Type = 1
FEATURE [PartDesign::Pocket] Pocket031
  BaseFeature = -> Pocket001
  Direction = (0,0,-1)
  Length = 5
  Length2 = 5
  Midplane = true
  Placement = pos=(0,0,0) rot=(0.57735,0.57735,0.57735;2.0944rad)
  Profile = -> Sketch070
  ReferenceAxis = -> Sketch070 [N_Axis]
  Suppressed = false
  Type = 1
FEATURE [PartDesign::Pocket] Pocket063
  BaseFeature = -> Pocket031
  Direction = (0,1,-2e-16)
  Length = 5
  Length2 = 5
  Placement = pos=(0,0,0) rot=(0.57735,0.57735,0.57735;2.0944rad)
  Profile = -> Sketch118
  ReferenceAxis = -> Sketch118 [N_Axis]
  Reversed = true
  Suppressed = false
  Type = 0
FEATURE [PartDesign::Body] Body011  label="pillar_bottom_material_0.30ansi"
  AllowCompound = false
  Group = -> [BaseBend060,Sketch011,Sketch012,WireFilter,WireFilter001,Pocket,Pocket001,Sketch070,Pocket031,Sketch118,Pocket063,pillar_bottom_LCS,Sketch289]
  Origin = -> Origin015
  Placement = pos=(18.3,54.5,0) rot=(0,0,1;1.5708rad)
  Tip = -> Pocket063
  expr: Placement = <<pillar_bottom_placement>>.AttachmentOffset
COMPONENT P52 — recipe-attached ("pillar_material_0.30ansi001", modeled in this document).
Construction recipe (the document's own serialized feature program — sketch geometry with constraints, then the solid features built on it; lengths are millimeters unless a unit is written):

FEATURE [PartDesign::SubShapeBinder] Binder002
  BindCopyOnChange = 0
  BindMode = 0
  ClaimChildren = true
  Fuse = false
  MakeFace = true
  OffsetFill = false
  OffsetIntersection = false
  OffsetJoinType = 0
  OffsetOpenResult = false
  PartialLoad = false
  Relative = false
  Support = -> [Sketch008]
  _Version = 2
FEATURE [PartDesign::FeaturePython] BaseBend004  label="pillar_BaseBend"  # WARN: FeaturePython — macro-defined, semantics opaque (R4)
  BendSide = 1
  BendSketch = -> Binder002
  MidPlane = false
  Reverse = false
  Suppressed = false
  length = 1594
  radius = 2
  thickness = 2
FEATURE [Sketcher::SketchObject] Sketch009
  ArcFitTolerance = 0
  AttachmentOffset = pos=(0,1594,0) rot=(0,0,1;0rad)
  AttachmentSupport = -> [XZ_Plane014]
  FullyConstrained = true
  MakeInternals = false
  MapMode = 5
  Placement = pos=(0,3.539e-13,1594) rot=(1,0,0;1.5708rad)
  expr: .AttachmentOffset.Base.y = BaseBend004.length
  expr: Constraints[15] = <<pillar_base_sketch>>.Constraints.width - (<<pillar_BaseBend>>.thickness + <<pillar_BaseBend>>.radius) * 2
  sketch-geometry (16):
    g0: LineSegment StartX=-14.3 StartY=0 StartZ=0 EndX=14.3 EndY=0 EndZ=0
    g1: LineSegment StartX=14.3 StartY=0 StartZ=0 EndX=14.3 EndY=2 EndZ=0
    g2: LineSegment StartX=14.3 StartY=2 StartZ=0 EndX=34.5 EndY=2 EndZ=0
    g3: LineSegment StartX=37.5 StartY=5 StartZ=0 EndX=37.5 EndY=87 EndZ=0
    g4: LineSegment StartX=34.5 StartY=90 StartZ=0 EndX=-34.5 EndY=90 EndZ=0
    g5: LineSegment StartX=-37.5 StartY=87 StartZ=0 EndX=-37.5 EndY=5 EndZ=0
    g6: LineSegment StartX=-34.5 StartY=2 StartZ=0 EndX=-14.3 EndY=2 EndZ=0
    g7: LineSegment StartX=-14.3 StartY=2 StartZ=0 EndX=-14.3 EndY=0 EndZ=0
    g8: ArcOfCircle CenterX=34.5 CenterY=5 CenterZ=0 NormalX=0 NormalY=0 NormalZ=1 AngleXU=0 Radius=3 StartAngle=4.71239 EndAngle=6.28319
    g9: GeomPoint [constr] X=37.5 Y=2 Z=0
    g10: ArcOfCircle CenterX=34.5 CenterY=87 CenterZ=0 NormalX=0 NormalY=0 NormalZ=1 AngleXU=0 Radius=3 StartAngle=1.02861e-11 EndAngle=1.5708
    g11: GeomPoint [constr] X=37.5 Y=90 Z=0
    g12: ArcOfCircle CenterX=-34.5 CenterY=87 CenterZ=0 NormalX=0 NormalY=0 NormalZ=1 AngleXU=0 Radius=3 StartAngle=1.5708 EndAngle=3.14159
    g13: GeomPoint [constr] X=-37.5 Y=90 Z=0
    g14: ArcOfCircle CenterX=-34.5 CenterY=5 CenterZ=0 NormalX=0 NormalY=0 NormalZ=1 AngleXU=0 Radius=3 StartAngle=3.14159 EndAngle=4.71239
    g15: GeomPoint [constr] X=-37.5 Y=2 Z=0
  constraints (38):
    c: PointOnObject(g0,g-1)
    c: Coincident(g0,g1)
    c: Vertical(g1)
    c: Coincident(g1,g2)
    c: Horizontal(g2)
    c: Vertical(g3)
    c: Vertical(g5)
    c: Horizontal(g6)
    c: Coincident(g6,g7)
    c: Vertical(g7)
    c: Coincident(g0,g7)
    c: Horizontal(g0)
    c: Symmetric(g6,g1,g-2)
    c: Symmetric(g11,g13,g-2)
    c: DistanceY(g1,g1) = 2
    c: DistanceX(g0,g0) = 28.6
    c: PointOnObject(g9,g2)
    c: PointOnObject(g9,g3)
    c: Tangent(g2,g8) = -1.5708
    c: Tangent(g3,g8) = -1.5708
    c: PointOnObject(g11,g3)
    c: PointOnObject(g11,g4)
    c: Tangent(g3,g10) = -1.5708
    c: Tangent(g4,g10) = -1.5708
    c: PointOnObject(g13,g4)
    c: PointOnObject(g13,g5)
    c: Tangent(g4,g12) = -1.5708
    c: Tangent(g5,g12) = -1.5708
    c: PointOnObject(g15,g5)
    c: PointOnObject(g15,g6)
    c: Tangent(g5,g14) = -1.5708
    c: Tangent(g6,g14) = -1.5708
    c: Equal(g14,g8)
    c: Equal(g14,g10)
    c: Equal(g14,g12)
    c: Radius(g14) = 3
    c: DistanceX(g13,g11) = 75
    c: DistanceY(g9,g11) = 88
FEATURE [PartDesign::SubShapeBinder] Binder072
  BindCopyOnChange = 0
  BindMode = 0
  ClaimChildren = true
  Context = -> Body010 [Binder072.]
  Fuse = false
  MakeFace = true
  OffsetFill = false
  OffsetIntersection = false
  OffsetJoinType = 0
  OffsetOpenResult = false
  PartialLoad = false
  Relative = true
  Support = -> [Body011[Pocket063.Sketch118.]]
  _Version = 2
FEATURE [PartDesign::Fillet] Fillet002
  Base = -> BaseBend004 [Edge10,Edge39,Edge41,Edge8]
  BaseFeature = -> BaseBend004
  Radius = 5
  SupportTransform = false
  Suppressed = false
  UseAllEdges = false
FEATURE [PartDesign::Pad] Pad
  BaseFeature = -> Fillet002
  Direction = (0,-1,2e-16)
  Length = 2
  Length2 = 10
  Profile = -> Sketch009
  ReferenceAxis = -> Sketch009 [N_Axis]
  Reversed = true
  Suppressed = false
  Type = 0
  expr: Length = <<pillar_BaseBend>>.thickness
FEATURE [PartDesign::Boolean] Boolean011
  BaseFeature = -> Pad
  Group = -> [Compound030]
  Refine = true
  Suppressed = false
  Type = 1
  UsePlacement = false
  expr: Group = <<pillar_cut1>>._self
FEATURE [PartDesign::Hole] Hole019
  BaseFeature = -> Boolean011
  CustomThreadClearance = 0
  Depth = 3405.27
  DepthType = 1
  Diameter = 3.4
  DrillForDepth = false
  DrillPoint = 1
  DrillPointAngle = 118
  HoleCutCountersinkAngle = 90
  HoleCutCustomValues = false
  HoleCutDepth = 0
  HoleCutDiameter = 6.1
  HoleCutType = 0
  ModelThread = false
  Profile = -> Binder072
  Suppressed = false
  Tapered = false
  TaperedAngle = 90
  ThreadClass = 0
  ThreadDepth = 3405.27
  ThreadDepthType = 0
  ThreadDirection = 0
  ThreadFit = 0
  ThreadSize = 0
  ThreadType = 0
  Threaded = false
  UseCustomThreadClearance = false
  expr: Diameter = <<Properties>>.rivet_d
FEATURE [PartDesign::Body] Body010  label="pillar_material_0.30ansi"
  AllowCompound = false
  Group = -> [Binder002,BaseBend004,Sketch009,Fillet002,Pad,Boolean011,Binder072,Hole019]
  Origin = -> Origin014
  Tip = -> Hole019
COMPONENT P53 — recipe-attached ("pillar_top_element_material_0.30ansi001", modeled in this document).
Construction recipe (the document's own serialized feature program — sketch geometry with constraints, then the solid features built on it; lengths are millimeters unless a unit is written):

FEATURE [Sketcher::SketchObject] Sketch013
  ArcFitTolerance = 0
  AttachmentSupport = -> [XY_Plane016]
  FullyConstrained = true
  MakeInternals = false
  MapMode = 5
  sketch-geometry (5):
    g0: LineSegment StartX=-36 StartY=25 StartZ=0 EndX=-36 EndY=0 EndZ=0
    g1: LineSegment StartX=-36 StartY=0 StartZ=0 EndX=36 EndY=0 EndZ=0
    g2: LineSegment StartX=36 StartY=0 StartZ=0 EndX=36 EndY=25 EndZ=0
    g3: LineSegment [constr] StartX=36 StartY=25 StartZ=0 EndX=-36 EndY=25 EndZ=0
    g4: GeomPoint [constr] X=0 Y=12.5 Z=0
  constraints (13):
    c: Coincident(g0,g1)
    c: Coincident(g1,g2)
    c: Coincident(g2,g3)
    c: Coincident(g3,g0)
    c: Horizontal(g1)
    c: Horizontal(g3)
    c: Vertical(g0)
    c: Vertical(g2)
    c: Symmetric(g1,g0,g4)
    c: PointOnObject(g4,g-2)
    c: PointOnObject(g1,g-1)
    c: DistanceY(g2,g2) = 25
    c: DistanceX(g1,g1) = 72
FEATURE [PartDesign::FeaturePython] BaseBend006  # WARN: FeaturePython — macro-defined, semantics opaque (R4)
  BendSide = 1
  BendSketch = -> Sketch013
  MidPlane = false
  Reverse = false
  Suppressed = false
  length = 84
  radius = 2
  thickness = 2
FEATURE [PartDesign::FeaturePython] Bend  # WARN: FeaturePython — macro-defined, semantics opaque (R4)
  AutoMiter = true
  BaseFeature = -> BaseBend006
  BendType = 1
  LengthList = [70]
  LengthSpec = 1
  NonperforationMaxLength = 5
  Perforate = false
  PerforationAngle = 0
  PerforationInitialLength = 5
  PerforationMaxLength = 5
  ReliefFactor = 0.7
  Suppressed = false
  UseReliefFactor = false
  angle = 90
  baseObject = -> BaseBend006 [Edge26]
  bendAList = [90]
  extend1 = 0
  extend2 = 0
  gap1 = 0
  gap2 = 0
  invert = true
  kfactor = 0.5
  length = 70
  maxExtendDist = 5
  minGap = 0.1
  minReliefGap = 1
  miterangle1 = 0
  miterangle2 = 0
  offset = 0
  radius = 2
  reliefType = 0
  reliefd = 1
  reliefw = 0.8
  sketchflip = false
  sketchinvert = false
  unfold = false
  expr: radius = BaseBend006.radius
FEATURE [Sketcher::SketchObject] Sketch066
  ArcFitTolerance = 0
  AttachmentSupport = -> [XY_Plane016]
  FullyConstrained = true
  MakeInternals = false
  MapMode = 5
  expr: Constraints[6] = <<Properties>>.rivet_d
  sketch-geometry (3):
    g0: Circle CenterX=0 CenterY=35 CenterZ=0 NormalX=0 NormalY=0 NormalZ=1 AngleXU=0 Radius=1.7
    g1: Circle CenterX=25 CenterY=60 CenterZ=0 NormalX=0 NormalY=0 NormalZ=1 AngleXU=0 Radius=1.7
    g2: Circle CenterX=-25 CenterY=60 CenterZ=0 NormalX=0 NormalY=0 NormalZ=1 AngleXU=0 Radius=1.7
  constraints (8):
    c: PointOnObject(g0,g-2)
    c: DistanceY(g0) = 35
    c: DistanceX(g1) = 25
    c: DistanceY(g1) = 60
    c: Equal(g0,g1)
    c: Equal(g0,g2)
    c: Diameter(g0) = 3.4
    c: Symmetric(g2,g1,g-2)
FEATURE [Sketcher::SketchObject] Sketch067
  ArcFitTolerance = 0
  AttachmentSupport = -> [XY_Plane016]
  FullyConstrained = true
  MakeInternals = false
  MapMode = 5
  sketch-geometry (13):
    g0: LineSegment StartX=-8.5 StartY=28 StartZ=0 EndX=-8.5 EndY=0 EndZ=0
    g1: LineSegment StartX=-8.5 StartY=0 StartZ=0 EndX=8.5 EndY=0 EndZ=0
    g2: LineSegment StartX=8.5 StartY=28 StartZ=0 EndX=-8.5 EndY=28 EndZ=0
    g3: GeomPoint [constr] X=0 Y=14 Z=0
    g4: LineSegment StartX=8.5 StartY=0 StartZ=0 EndX=14 EndY=0 EndZ=0
    g5: LineSegment StartX=8.5 StartY=20.9904 StartZ=0 EndX=8.5 EndY=28 EndZ=0
    g6: ArcOfCircle CenterX=8.5 CenterY=8 CenterZ=0 NormalX=0 NormalY=0 NormalZ=1 AngleXU=0 Radius=7.5 StartAngle=0 EndAngle=1.0472
    g7: ArcOfCircle CenterX=16 CenterY=20.9904 CenterZ=0 NormalX=0 NormalY=0 NormalZ=1 AngleXU=0 Radius=7.5 StartAngle=3.14159 EndAngle=4.18879
    g8: LineSegment StartX=14 StartY=0 StartZ=0 EndX=14 EndY=4 EndZ=0
    g9: LineSegment [constr] StartX=14 StartY=4 StartZ=0 EndX=14 EndY=10 EndZ=0
    g10: LineSegment StartX=16 StartY=6 StartZ=0 EndX=16 EndY=8 EndZ=0
    g11: ArcOfCircle CenterX=15 CenterY=4 CenterZ=0 NormalX=0 NormalY=0 NormalZ=1 AngleXU=0 Radius=1 StartAngle=1.5708 EndAngle=3.14159
    g12: ArcOfCircle CenterX=15 CenterY=6 CenterZ=0 NormalX=0 NormalY=0 NormalZ=1 AngleXU=0 Radius=1 StartAngle=4.71239 EndAngle=6.28319
  constraints (34):
    c: Coincident(g0,g1)
    c: Coincident(g1,g4)
    c: Coincident(g5,g2)
    c: Coincident(g2,g0)
    c: Horizontal(g1)
    c: Vertical(g0)
    c: Symmetric(g1,g0,g3)
    c: PointOnObject(g3,g-2)
    c: PointOnObject(g1,g-1)
    c: DistanceX(g2,g2) = 17
    c: DistanceY(g4,g5) = 28
    c: Coincident(g4,g8)
    c: Vertical(g5)
    c: Horizontal(g4)
    c: DistanceX(g4,g4) = 5.5
    c: DistanceY(g8,g9) = 10
    c: Symmetric(g2,g0,g-2)
    c: Tangent(g7,g6) = 1.5708
    c: Tangent(g7,g5) = 1.5708
    c: PointOnObject(g6,g5)
    c: Equal(g6,g7)
    c: Coincident(g8,g9)
    c: Vertical(g8)
    c: Vertical(g9)
    c: DistanceY(g8,g8) = 4
    c: Vertical(g10)
    c: DistanceX(g10) = 16
    c: Tangent(g11,g8) = 1.5708
    c: Tangent(g12,g11) = 1.5708
    c: Tangent(g12,g10) = -1.5708
    c: Equal(g12,g11)
    c: Tangent(g6,g10) = -1.5708
    c: Vertical(g11,g11)
    c: DistanceY(g10,g10) = 2
FEATURE [Sketcher::SketchObject] Sketch073
  ArcFitTolerance = 0
  AttachmentSupport = -> [YZ_Plane016]
  FullyConstrained = true
  MakeInternals = false
  MapMode = 5
  Placement = pos=(0,0,0) rot=(0.57735,0.57735,0.57735;2.0944rad)
  expr: Constraints[5] = <<Properties>>.rivet_d
  sketch-geometry (2):
    g0: Circle CenterX=10 CenterY=80 CenterZ=0 NormalX=0 NormalY=0 NormalZ=1 AngleXU=0 Radius=1.7
    g1: Circle CenterX=10 CenterY=10 CenterZ=0 NormalX=0 NormalY=0 NormalZ=1 AngleXU=0 Radius=1.7
  constraints (6):
    c: Vertical(g1,g0)
    c: DistanceX(g1) = 10
    c: DistanceY(g0) = 80
    c: DistanceY(g1) = 10
    c: Equal(g1,g0)
    c: Diameter(g1) = 3.4
FEATURE [PartDesign::Fillet] Fillet001
  Base = -> Bend [Edge12,Edge60,Edge14,Edge64,Edge41,Edge59]
  BaseFeature = -> Bend
  Radius = 5
  SupportTransform = false
  Suppressed = false
  UseAllEdges = false
FEATURE [PartDesign::Hole] Hole005
  BaseFeature = -> Fillet001
  CustomThreadClearance = 0
  Depth = 286.27
  DepthType = 1
  Diameter = 3.4
  DrillForDepth = false
  DrillPoint = 1
  DrillPointAngle = 118
  HoleCutCountersinkAngle = 90
  HoleCutCustomValues = false
  HoleCutDepth = 0
  HoleCutDiameter = 6.1
  HoleCutType = 0
  ModelThread = false
  Profile = -> Sketch066
  Reversed = true
  Suppressed = false
  Tapered = false
  TaperedAngle = 90
  ThreadClass = 0
  ThreadDepth = 286.27
  ThreadDepthType = 0
  ThreadDirection = 0
  ThreadFit = 0
  ThreadSize = 0
  ThreadType = 0
  Threaded = false
  UseCustomThreadClearance = false
  expr: Diameter = <<Properties>>.rivet_d
FEATURE [PartDesign::Pocket] Pocket030
  BaseFeature = -> Hole005
  Direction = (0,0,-1)
  Length = 5
  Length2 = 5
  Profile = -> Sketch067
  ReferenceAxis = -> Sketch067 [N_Axis]
  Reversed = true
  Suppressed = false
  Type = 0
FEATURE [PartDesign::Pocket] Pocket034
  BaseFeature = -> Pocket030
  Direction = (-1,0,0)
  Length = 5
  Length2 = 5
  Midplane = true
  Profile = -> Sketch073
  ReferenceAxis = -> Sketch073 [N_Axis]
  Suppressed = false
  Type = 1
FEATURE [PartDesign::SubShapeBinder] Binder074
  BindCopyOnChange = 0
  BindMode = 0
  ClaimChildren = false
  Context = -> Body012 [Binder074.]
  Fuse = false
  MakeFace = true
  OffsetFill = false
  OffsetIntersection = false
  OffsetJoinType = 0
  OffsetOpenResult = false
  PartialLoad = false
  Relative = true
  Support = -> [Body010[Boolean011.Edge138,Boolean011.Edge140,Boolean011.Edge152]]
  _Version = 2
FEATURE [PartDesign::Pocket] Pocket065
  BaseFeature = -> Pocket034
  Direction = (0,-1,4e-16)
  Length = 5
  Length2 = 5
  Profile = -> Binder074
  Reversed = true
  Suppressed = false
  Type = 0
FEATURE [PartDesign::Body] Body012  label="pillar_top_element_material_0.30ansi"
  AllowCompound = false
  Group = -> [Sketch013,BaseBend006,Bend,Sketch066,Fillet001,Hole005,Sketch067,Pocket030,Sketch073,Pocket034,Binder074,Pocket065]
  Origin = -> Origin016
  Placement = pos=(0,2,1594) rot=(0,0,1;0rad)
  Tip = -> Pocket065
COMPONENT P54 — recipe-attached ("top_dec_corner_material_0.30ansi001", modeled in this document).
Construction recipe (the document's own serialized feature program — sketch geometry with constraints, then the solid features built on it; lengths are millimeters unless a unit is written):

FEATURE [Sketcher::SketchObject] Sketch119
  ArcFitTolerance = 0
  AttachmentSupport = -> [XY_Plane018]
  FullyConstrained = true
  MakeInternals = false
  MapMode = 5
  sketch-geometry (2):
    g0: LineSegment StartX=37.5 StartY=-1.5 StartZ=0 EndX=-37.5 EndY=-1.5 EndZ=0
    g1: LineSegment StartX=-37.5 StartY=-1.5 StartZ=0 EndX=-37.5 EndY=27 EndZ=0
  constraints (6):
    c: Coincident(g1,g0)
    c: Vertical(g1)
    c: DistanceY(g0) = -1.5
    c: Symmetric(g0,g0,g-2)
    c: DistanceX(g0,g0) = 75
    c: DistanceY(g1) = 27
FEATURE [PartDesign::FeaturePython] BaseBend029  # WARN: FeaturePython — macro-defined, semantics opaque (R4)
  BendSide = 1
  BendSketch = -> Sketch119
  MidPlane = false
  Placement = pos=(0,0,1588) rot=(0,0,1;0rad)
  Reverse = false
  Suppressed = false
  length = 96
  radius = 2
  thickness = 0.5
FEATURE [Sketcher::SketchObject] Sketch120
  ArcFitTolerance = 0
  AttachmentOffset = pos=(0,1588,0) rot=(0,0,1;0rad)
  AttachmentSupport = -> [XZ_Plane018]
  FullyConstrained = true
  MakeInternals = false
  MapMode = 5
  Placement = pos=(0,3.526e-13,1588) rot=(1,0,0;1.5708rad)
  expr: .AttachmentOffset.Base.y = BaseBend029.Placement.Base.z
  sketch-geometry (5):
    g0: ArcOfCircle CenterX=-35.5 CenterY=13.8267 CenterZ=0 NormalX=0 NormalY=0 NormalZ=1 AngleXU=0 Radius=13.8267 StartAngle=4.71239 EndAngle=5.38367
    g1: ArcOfCircle CenterX=-18.3 CenterY=-7.82667 CenterZ=0 NormalX=0 NormalY=0 NormalZ=1 AngleXU=0 Radius=13.8267 StartAngle=1.5708 EndAngle=2.24207
    g2: LineSegment StartX=-18.3 StartY=6 StartZ=0 EndX=40 EndY=6 EndZ=0
    g3: LineSegment StartX=40 StartY=6 StartZ=0 EndX=40 EndY=0 EndZ=0
    g4: LineSegment StartX=40 StartY=0 StartZ=0 EndX=-35.5 EndY=1.42e-14 EndZ=0
  constraints (15):
    c: PointOnObject(g0,g-1)
    c: Horizontal(g2)
    c: Coincident(g3,g2)
    c: PointOnObject(g3,g-1)
    c: Vertical(g3)
    c: Coincident(g4,g3)
    c: Coincident(g4,g0)
    c: Tangent(g4,g0)
    c: Equal(g0,g1)
    c: DistanceX(g0) = -35.5
    c: Tangent(g2,g1) = 1.5708
    c: Tangent(g1,g0) = 1.5708
    c: DistanceY(g3,g3) = 6
    c: DistanceX(g1) = -18.3
    c: DistanceX(g3) = 40
FEATURE [PartDesign::Pocket] Pocket064
  BaseFeature = -> BaseBend029
  Direction = (0,1,-2e-16)
  Length = 5
  Length2 = 5
  Midplane = true
  Placement = pos=(0,0,1588) rot=(0,0,1;0rad)
  Profile = -> Sketch120
  ReferenceAxis = -> Sketch120 [N_Axis]
  Suppressed = false
  Type = 1
FEATURE [PartDesign::Fillet] Fillet004
  Base = -> Pocket064 [Edge25,Edge31,Edge8,Edge10]
  BaseFeature = -> Pocket064
  Placement = pos=(0,0,1588) rot=(0,0,1;0rad)
  Radius = 3
  SupportTransform = false
  Suppressed = false
  UseAllEdges = false
FEATURE [PartDesign::Boolean] Boolean014
  BaseFeature = -> Fillet004
  Group = -> [Compound044]
  Suppressed = false
  Type = 1
  UsePlacement = false
FEATURE [PartDesign::SubShapeBinder] Binder073
  BindCopyOnChange = 0
  BindMode = 0
  ClaimChildren = false
  Context = -> Link025 [Binder073.]
  Fuse = false
  MakeFace = true
  OffsetFill = false
  OffsetIntersection = false
  OffsetJoinType = 0
  OffsetOpenResult = false
  PartialLoad = false
  Relative = true
  Support = -> [Body012[Pocket034.Sketch073.]]
  _Version = 2
FEATURE [PartDesign::Hole] Hole020
  BaseFeature = -> Boolean014
  CustomThreadClearance = 0
  Depth = 253.566
  DepthType = 1
  Diameter = 3.4
  DrillForDepth = false
  DrillPoint = 1
  DrillPointAngle = 118
  HoleCutCountersinkAngle = 90
  HoleCutCustomValues = false
  HoleCutDepth = 0
  HoleCutDiameter = 6.1
  HoleCutType = 0
  ModelThread = false
  Profile = -> Binder073
  Suppressed = false
  Tapered = false
  TaperedAngle = 90
  ThreadClass = 0
  ThreadDepth = 253.566
  ThreadDepthType = 0
  ThreadDirection = 0
  ThreadFit = 0
  ThreadSize = 0
  ThreadType = 0
  Threaded = false
  UseCustomThreadClearance = false
  expr: Diameter = <<Properties>>.rivet_d
FEATURE [PartDesign::Body] Body014  label="top_dec_corner_material_0.30ansi"
  AllowCompound = false
  Group = -> [Sketch119,BaseBend029,Sketch120,Pocket064,Fillet004,Boolean014,Binder073,Hole020]
  Origin = -> Origin018
  Tip = -> Hole020
COMPONENT P55 — recipe-attached ("dec_corner_material_0.30ansi001", modeled in this document).
Construction recipe (the document's own serialized feature program — sketch geometry with constraints, then the solid features built on it; lengths are millimeters unless a unit is written):

FEATURE [PartDesign::SubShapeBinder] Binder035
  BindCopyOnChange = 0
  BindMode = 0
  ClaimChildren = true
  Fuse = false
  MakeFace = true
  OffsetFill = false
  OffsetIntersection = false
  OffsetJoinType = 0
  OffsetOpenResult = false
  PartialLoad = false
  Relative = false
  Support = -> [Sketch056]
  _Version = 2
FEATURE [PartDesign::FeaturePython] BaseBend017  # WARN: FeaturePython — macro-defined, semantics opaque (R4)
  BendSide = 0
  BendSketch = -> Binder035
  MidPlane = false
  Placement = pos=(0,0,481) rot=(0,0,1;0rad)
  Reverse = false
  Suppressed = false
  length = 1113
  radius = 2
  thickness = 0.5
FEATURE [PartDesign::Fillet] Fillet003
  Base = -> BaseBend017 [Edge23,Edge10,Edge25,Edge8]
  BaseFeature = -> BaseBend017
  Placement = pos=(0,0,481) rot=(0,0,1;0rad)
  Radius = 5
  SupportTransform = false
  Suppressed = false
  UseAllEdges = false
FEATURE [PartDesign::Boolean] Boolean012
  BaseFeature = -> Fillet003
  Group = -> [Compound032]
  Suppressed = false
  Type = 1
  UsePlacement = false
  expr: Group = <<dec_corner_cut1>>._self
FEATURE [PartDesign::Body] Body013  label="dec_corner_material_0.30ansi"
  AllowCompound = false
  Group = -> [Binder035,BaseBend017,Fillet003,Boolean012]
  Origin = -> Origin017
  Tip = -> Boolean012
COMPONENT P56 — recipe-attached ("basement_amplifier_material_0.30ansi002", modeled in this document).
Construction recipe (the document's own serialized feature program — sketch geometry with constraints, then the solid features built on it; lengths are millimeters unless a unit is written):

FEATURE [Sketcher::SketchObject] Sketch167  label="basement_amplifier_sketch"
  ArcFitTolerance = 0
  AttachmentSupport = -> [XY_Plane078]
  FullyConstrained = true
  MakeInternals = false
  MapMode = 5
  sketch-geometry (10):
    g0: LineSegment StartX=-25 StartY=320.166 StartZ=0 EndX=25 EndY=320.166 EndZ=0
    g1: LineSegment StartX=80 StartY=46.188 StartZ=0 EndX=0 EndY=0 EndZ=0
    g2: LineSegment StartX=0 StartY=0 StartZ=0 EndX=-80 EndY=46.188 EndZ=0
    g3: LineSegment StartX=25 StartY=320.166 StartZ=0 EndX=79.5375 EndY=48.492 EndZ=0
    g4: LineSegment StartX=79.5375 StartY=48.492 StartZ=0 EndX=80 EndY=46.188 EndZ=0
    g5: LineSegment StartX=-80 StartY=46.188 StartZ=0 EndX=-79.5375 EndY=48.492 EndZ=0
    g6: LineSegment StartX=-79.5375 StartY=48.492 StartZ=0 EndX=-25 EndY=320.166 EndZ=0
    g7: LineSegment [constr] StartX=-79.7343 StartY=47.5116 StartZ=0 EndX=-83.6561 EndY=48.2988 EndZ=0
    g8: LineSegment [constr] StartX=-83.6561 StartY=48.2988 StartZ=0 EndX=-81.0134 EndY=45.2961 EndZ=0
    g9: LineSegment [constr] StartX=-81.0134 StartY=45.2961 StartZ=0 EndX=-80 EndY=46.188 EndZ=0
  constraints (27):
    c: Coincident(g2,g5)
    c: Coincident(g6,g0)
    c: Coincident(g0,g3)
    c: Coincident(g4,g1)
    c: Symmetric(g1,g2,g-2)
    c: Symmetric(g0,g6,g-2)
    c: DistanceX(g0,g0) = 50
    c: DistanceY(g6) = 320.166  'length'
    c: DistanceX(g2,g1) = 160
    c: Coincident(g1,g2)
    c: Coincident(g3,g4)
    c: Symmetric(g5,g3,g-2)
    c: Coincident(g8,g7)
    c: Perpendicular(g5,g7)
    c: Equal(g8,g7)
    c: Distance(g7) = 4
    c: PointOnObject(g7,g5)
    c: Coincident(g6,g5)
    c: Distance(g7,g5) = 1
    c: Distance(g2) = 92.376  'inner_r'
    c: Angle(g1) = -2.61799
    c: Coincident(g9,g8)
    c: Coincident(g9,g2)
    c: Symmetric(g8,g7,g2)
    c: Parallel(g5,g6)
    c: Coincident(g1,g-1)
    c: Angle(g5,g9) = 2.49062  'connection_angle'
FEATURE [PartDesign::FeaturePython] BaseBend043  # WARN: FeaturePython — macro-defined, semantics opaque (R4)
  BendSide = 0
  BendSketch = -> Sketch167
  MidPlane = false
  Reverse = false
  Suppressed = false
  length = 100
  radius = 2
  thickness = 2
FEATURE [PartDesign::FeaturePython] Bend025  # WARN: FeaturePython — macro-defined, semantics opaque (R4)
  AutoMiter = false
  BaseFeature = -> BaseBend043
  BendType = 0
  LengthList = [100]
  LengthSpec = 0
  NonperforationMaxLength = 5
  Perforate = false
  PerforationAngle = 0
  PerforationInitialLength = 5
  PerforationMaxLength = 5
  ReliefFactor = 0.7
  Suppressed = false
  UseReliefFactor = false
  angle = 90
  baseObject = -> BaseBend043 [Edge21,Edge7]
  bendAList = [90]
  extend1 = 0
  extend2 = 0
  gap1 = 0
  gap2 = 0
  invert = true
  kfactor = 0.5
  length = 100
  maxExtendDist = 5
  minGap = 0.1
  minReliefGap = 1
  miterangle1 = 18.649
  miterangle2 = 18.649
  offset = 0
  radius = 2
  reliefType = 0
  reliefd = 1
  reliefw = 0.8
  sketchflip = false
  sketchinvert = false
  unfold = false
  expr: miterangle1 = 90 deg - Sketch167.Constraints.connection_angle / 2
  expr: miterangle2 = miterangle1
  expr: radius = BaseBend043.radius
FEATURE [Sketcher::SketchObject] Sketch170
  ArcFitTolerance = 0
  AttachmentSupport = -> [YZ_Plane078]
  FullyConstrained = false
  MakeInternals = false
  MapMode = 5
  Placement = pos=(0,0,0) rot=(0.57735,0.57735,0.57735;2.0944rad)
  expr: Constraints[10] = <<basement_amplifier_sketch>>.Constraints.length
  sketch-geometry (11):
    g0: LineSegment StartX=320.166 StartY=-15 StartZ=0 EndX=320.166 EndY=2 EndZ=0
    g1: LineSegment StartX=320.166 StartY=2 StartZ=0 EndX=0 EndY=2 EndZ=0
    g2: LineSegment StartX=0 StartY=2 StartZ=0 EndX=0 EndY=-60 EndZ=0
    g3: LineSegment StartX=0 StartY=-60 StartZ=0 EndX=125.378 EndY=-25.2665 EndZ=0
    g4: LineSegment StartX=133.266 StartY=-24 StartZ=0 EndX=320.166 EndY=-15 EndZ=0
    g5: ArcOfCircle CenterX=135 CenterY=-60 CenterZ=0 NormalX=0 NormalY=0 NormalZ=1 AngleXU=0 Radius=36.0417 StartAngle=1.61891 EndAngle=1.84105
    g6: GeomPoint [constr] X=129.251 Y=-24.1933 Z=0
    g7: LineSegment StartX=-219.815 StartY=310.193 StartZ=0 EndX=564.966 EndY=310.193 EndZ=0
    g8: LineSegment StartX=564.966 StartY=310.193 StartZ=0 EndX=564.966 EndY=-309.063 EndZ=0
    g9: LineSegment StartX=564.966 StartY=-309.063 StartZ=0 EndX=-219.815 EndY=-309.063 EndZ=0
    g10: LineSegment StartX=-219.815 StartY=-309.063 StartZ=0 EndX=-219.815 EndY=310.193 EndZ=0
  constraints (27):
    c: Vertical(g0)
    c: Coincident(g0,g1)
    c: Horizontal(g1)
    c: PointOnObject(g2,g-2)
    c: Coincident(g4,g0)
    c: Coincident(g2,g1)
    c: Vertical(g2)
    c: DistanceY(g-1,g1) = 2
    c: DistanceY(g0,g1) = 17
    c: DistanceY(g2) = -60
    c: DistanceX(g1,g1) = 320.166
    c: PointOnObject(g6,g4)
    c: PointOnObject(g6,g3)
    c: Tangent(g4,g5) = 1.5708
    c: Tangent(g3,g5) = 1.5708
    c: Coincident(g7,g8)
    c: Coincident(g8,g9)
    c: Coincident(g9,g10)
    c: Coincident(g10,g7)
    c: Horizontal(g7)
    c: Horizontal(g9)
    c: Vertical(g8)
    c: Vertical(g10)
    c: DistanceY(g4) = -24
    c: DistanceX(g5) = 135
    c: Coincident(g3,g2)
    c: Horizontal(g5,g2)
FEATURE [PartDesign::Plane] DatumPlane005
  AttachmentOffset = pos=(0,0,0) rot=(0,-1,0;1.5708rad)
  AttachmentSupport = -> [Sketch167]
  Length = 647.453
  MapMode = 7
  Placement = pos=(-79.5375,48.492,0) rot=(0.501242,-0.611865,-0.611865;2.21231rad)
  ResizeMode = 0
  Width = 88.0953
FEATURE [PartDesign::Line] DatumLine003
  AttacherType = Attacher::AttachEngineLine
  AttachmentOffset = pos=(0,0,0) rot=(0,1,0;1.5708rad)
  AttachmentSupport = -> [Sketch170]
  Length = 20
  MapMode = 24
  Placement = pos=(0,0,-60) rot=(0,1,0;1.5708rad)
  ResizeMode = 0
FEATURE [PartDesign::Line] DatumLine004
  AttacherType = Attacher::AttachEngineLine
  AttachmentOffset = pos=(0,0,0) rot=(0,1,0;1.5708rad)
  AttachmentSupport = -> [Sketch170]
  Length = 20
  MapMode = 24
  Placement = pos=(0,133.266,-24) rot=(0.58639,0.558832,0.58639;2.1224rad)
  ResizeMode = 0
FEATURE [Sketcher::SketchObject] Sketch173
  ArcFitTolerance = 0
  AttachmentOffset = pos=(0,0,4) rot=(0,0,1;0rad)
  AttachmentSupport = -> [DatumPlane005]
  ExternalGeometry = -> [Sketch167]
  FullyConstrained = false
  MakeInternals = false
  MapMode = 5
  Placement = pos=(-83.4592,49.2793,0) rot=(-0.501242,0.611865,0.611865;4.07087rad)
  sketch-geometry (9):
    g0: LineSegment StartX=49.4595 StartY=-30.4174 StartZ=0 EndX=49.4595 EndY=2 EndZ=0
    g1: LineSegment StartX=-86.4657 StartY=-24 StartZ=0 EndX=-277.094 EndY=-15 EndZ=0
    g2: LineSegment StartX=-277.094 StartY=-15 StartZ=0 EndX=-277.094 EndY=2 EndZ=0
    g3: LineSegment StartX=-277.094 StartY=2 StartZ=0 EndX=49.4595 EndY=2 EndZ=0
    g4: LineSegment StartX=-568.045 StartY=-343.581 StartZ=0 EndX=236.236 EndY=-343.581 EndZ=0
    g5: LineSegment StartX=236.236 StartY=-343.581 StartZ=0 EndX=236.236 EndY=220.397 EndZ=0
    g6: LineSegment StartX=236.236 StartY=220.397 StartZ=0 EndX=-568.045 EndY=220.397 EndZ=0
    g7: LineSegment StartX=-568.045 StartY=220.397 StartZ=0 EndX=-568.045 EndY=-343.581 EndZ=0
    g8: LineSegment StartX=-86.4657 StartY=-24 StartZ=0 EndX=49.4595 EndY=-30.4174 EndZ=0
  constraints (22):
    c: Coincident(g2,g1)
    c: Vertical(g2)
    c: Coincident(g3,g2)
    c: Horizontal(g3)
    c: Coincident(g3,g0)
    c: DistanceY(g0) = 2
    c: DistanceY(g1) = -15
    c: Coincident(g4,g5)
    c: Coincident(g5,g6)
    c: Coincident(g6,g7)
    c: Coincident(g7,g4)
    c: Horizontal(g4)
    c: Horizontal(g6)
    c: Vertical(g5)
    c: Vertical(g7)
    c: PointOnObject(g-5,g2)
    c: Coincident(g1,g-4) = -1.5708
    c: Coincident(g8,g1)
    c: Coincident(g8,g0)
    c: Parallel(g8,g1)
    c: Vertical(g0)
    c: PointOnObject(g-3,g0)
FEATURE [PartDesign::Pocket] Pocket104
  BaseFeature = -> Bend025
  Direction = (0.98044,-0.19682,0)
  Length = 2
  Length2 = 5
  Profile = -> Sketch173
  ReferenceAxis = -> Sketch173 [N_Axis]
  Suppressed = false
  Type = 0
FEATURE [PartDesign::Fillet] Fillet011
  Base = -> Pocket104 [Edge57,Edge56]
  BaseFeature = -> Pocket104
  Radius = 10
  SupportTransform = false
  Suppressed = false
  UseAllEdges = false
FEATURE [PartDesign::SubShapeBinder] Binder118
  BindCopyOnChange = 0
  BindMode = 0
  ClaimChildren = false
  Context = -> Body105 [Binder118.]
  Fuse = false
  MakeFace = true
  OffsetFill = false
  OffsetIntersection = false
  OffsetJoinType = 0
  OffsetOpenResult = false
  PartialLoad = false
  Relative = true
  Support = -> [Body006[Binder069.]]
  _Version = 2
FEATURE [PartDesign::SubShapeBinder] Binder119
  BindCopyOnChange = 0
  BindMode = 0
  ClaimChildren = false
  Context = -> Body105 [Binder119.]
  Fuse = false
  MakeFace = true
  OffsetFill = false
  OffsetIntersection = false
  OffsetJoinType = 0
  OffsetOpenResult = false
  PartialLoad = false
  Relative = true
  Support = -> [Body006[Pocket061.Sketch112.]]
  _Version = 2
FEATURE [PartDesign::Pocket] Pocket108
  BaseFeature = -> Fillet011
  Direction = (0,0,-1)
  Length = 5
  Length2 = 5
  Midplane = true
  Profile = -> Binder119
  Suppressed = false
  Type = 1
FEATURE [Sketcher::SketchObject] Sketch175
  ArcFitTolerance = 0
  AttachmentSupport = -> [XY_Plane078]
  ExternalGeometry = -> [Sketch167]
  FullyConstrained = true
  MakeInternals = false
  MapMode = 5
  sketch-geometry (6):
    g0: Circle CenterX=43.3161 CenterY=155 CenterZ=0 NormalX=0 NormalY=0 NormalZ=1 AngleXU=0 Radius=2.55
    g1: Circle CenterX=-43.3161 CenterY=155 CenterZ=0 NormalX=0 NormalY=0 NormalZ=1 AngleXU=0 Radius=2.55
    g2: Circle CenterX=63.3907 CenterY=55 CenterZ=0 NormalX=0 NormalY=0 NormalZ=1 AngleXU=0 Radius=2.55
    g3: Circle CenterX=-63.3907 CenterY=55 CenterZ=0 NormalX=0 NormalY=0 NormalZ=1 AngleXU=0 Radius=2.55
    g4: LineSegment [constr] StartX=45.8162 StartY=155.502 StartZ=0 EndX=57.5815 EndY=157.864 EndZ=0
    g5: LineSegment [constr] StartX=65.8909 StartY=55.5019 StartZ=0 EndX=77.6561 EndY=57.8637 EndZ=0
  constraints (18):
    c: Distance(g0,g-3) = 12
    c: Diameter(g0) = 5.1
    c: Equal(g1,g0)
    c: Symmetric(g1,g0,g-2)
    c: DistanceY(g0) = 155
    c: Symmetric(g2,g3,g-2)
    c: Equal(g2,g3)
    c: Equal(g3,g0)
    c: PointOnObject(g4,g0)
    c: PointOnObject(g4,g-3)
    c: PointOnObject(g5,g2)
    c: PointOnObject(g5,g-3)
    c: Perpendicular(g5,g-3)
    c: PointOnObject(g2,g5)
    c: Equal(g5,g4)
    c: PointOnObject(g0,g4)
    c: Perpendicular(g-3,g4)
    c: DistanceY(g2) = 55
FEATURE [PartDesign::Pocket] Pocket109
  BaseFeature = -> Pocket108
  Direction = (0,0,-1)
  Length = 5
  Length2 = 5
  Midplane = true
  Profile = -> Sketch175
  ReferenceAxis = -> Sketch175 [N_Axis]
  Suppressed = false
  Type = 1
FEATURE [PartDesign::Mirrored] Mirrored010
  BaseFeature = -> Pocket109
  MirrorPlane = -> YZ_Plane078
  Originals = -> [Pocket104,Fillet011]
  Suppressed = false
  TransformMode = 0
FEATURE [PartDesign::FeatureAdditivePython] PDW_Common_Add  # link proxy (typed FeaturePython)
  BaseFeature = -> Mirrored010
  Body = Body105
  ClaimChildren = false
  EditPlacementAdjustments = false
  Enabled = 0
  LinkedObject = -> Mirrored010
  MeshTolerance = 0.1
  PatternBase = -> Pocket109
  PatternBaseOffset = 0
  PatternBaseScale = 1
  PatternBaseScaleXYZ = (1,1,1)
  PatternOffsetCut = false
  PatternOffsetIntersection = false
  PatternOffsetJoin = 0
  PatternOffsetMode = 0
  PatternOffsetSelfIntersection = false
  PatternOperation = 3
  PatternOperationDefault = Common
  PatternScaleCut = false
  PatternShapeOffset = 0
  PatternShapeScale = 1
  PatternShapeScaleXYZ = (1,1,1)
  PatternTool = -> Mirrored010
  PatternToolOffset = 0
  PatternToolScale = 1
  PatternToolScaleXYZ = (1,1,1)
  RefineMesh = true
  ShapeManagement = 0
  ShowMeshProps = false
  ShowOffsetProps = false
  ShowScaleProps = false
  ShowWarnings = true
  Suppressed = false
  TipBase = -> Mirrored010
  TipBaseOffset = 0
  TipBaseScale = 1
  TipBaseScaleXYZ = (1,1,1)
  TipOffsetCut = false
  TipOffsetIntersection = false
  TipOffsetJoin = 0
  TipOffsetMode = 0
  TipOffsetSelfIntersection = false
  TipOperation = 4
  TipOperationDefault = Common
  TipScaleCut = false
  TipShapeOffset = 0
  TipShapeScale = 1
  TipShapeScaleXYZ = (1,1,1)
  TipTool = -> Mirrored010
  TipToolOffset = 0
  TipToolScale = 1
  TipToolScaleXYZ = (1,1,1)
  Type = Additive
  UsePatternBaseAddSubShape = false
  UsePatternToolAddSubShape = true
  UseTipBaseAddSubShape = false
  UseTipToolAddSubShape = true
  Version = 0.2023.08.13
FEATURE [PartDesign::PolarPattern] PolarPattern006
  Angle = 360
  Axis = -> Z_Axis078
  BaseFeature = -> PDW_Common_Add
  Mode = 0
  Occurrences = 3
  Offset = 120
  Originals = -> [PDW_Common_Add]
  Refine = true
  Suppressed = false
  TransformMode = 0
FEATURE [PartDesign::Pocket] Pocket107
  BaseFeature = -> PolarPattern006
  Direction = (0,0,-1)
  Length = 5
  Length2 = 5
  Midplane = true
  Profile = -> Binder118
  Suppressed = false
  Type = 1
FEATURE [PartDesign::Boolean] Boolean028
  BaseFeature = -> Pocket107
  Group = -> [Compound070]
  Suppressed = false
  Type = 1
  UsePlacement = false
FEATURE [PartDesign::CoordinateSystem] Local_CS021  label="basement_top_amplifier_bottom_LCS"
  AttacherType = Attacher::AttachEngine3D
  AttachmentSupport = -> [XY_Plane078]
  MapMode = 5
FEATURE [PartDesign::CoordinateSystem] Local_CS022  label="basement_top_amplifier_top_LCS"
  AttacherType = Attacher::AttachEngine3D
  AttachmentOffset = pos=(0,0,2) rot=(0,0,1;0rad)
  AttachmentSupport = -> [XY_Plane078]
  MapMode = 5
  Placement = pos=(0,0,2) rot=(0,0,1;0rad)
FEATURE [PartDesign::Body] Body105  label="basement_top_amplifier_material_0.50ansi"
  AllowCompound = false
  Group = -> [Sketch167,BaseBend043,Bend025,Pocket104,Fillet011,Binder119,Sketch170,DatumPlane005,DatumLine003,DatumLine004,Sketch173,Pocket108,Sketch175,Pocket109,Mirrored010,PDW_Common_Add,PolarPattern006,Binder118,Pocket107,Boolean028,Local_CS021,Local_CS022]
  Origin = -> Origin078
  Tip = -> Boolean028
COMPONENT P57 — recipe-attached ("basement_proxy001", modeled in this document).
Construction recipe (the document's own serialized feature program — sketch geometry with constraints, then the solid features built on it; lengths are millimeters unless a unit is written):

FEATURE [PartDesign::SubShapeBinder] Binder006
  BindCopyOnChange = 0
  BindMode = 0
  ClaimChildren = true
  Context = -> Body008 [Binder006.]
  Fuse = false
  MakeFace = true
  Offset = 2
  OffsetFill = false
  OffsetIntersection = false
  OffsetJoinType = 0
  OffsetOpenResult = false
  PartialLoad = false
  Relative = false
  Support = -> [Array003]
  _Version = 2
FEATURE [PartDesign::Pad] Pad003
  Direction = (0,0,1)
  Length = 3
  Length2 = 10
  Profile = -> Binder006
  Suppressed = false
  Type = 0
FEATURE [PartDesign::SubShapeBinder] Binder129
  BindCopyOnChange = 0
  BindMode = 0
  ClaimChildren = false
  Context = -> Link028 [Binder129.]
  Fuse = false
  MakeFace = true
  OffsetFill = false
  OffsetIntersection = false
  OffsetJoinType = 0
  OffsetOpenResult = false
  PartialLoad = false
  Relative = true
  Support = -> [Link005[Hole.Binder001.]]
  _Version = 2
FEATURE [PartDesign::Boolean] Boolean021
  BaseFeature = -> Pad003
  Group = -> [Compound063]
  Suppressed = false
  Type = 1
  UsePlacement = false
FEATURE [PartDesign::CoordinateSystem] Local_CS017  label="basement_top_proxy_bottom_LCS"
  AttacherType = Attacher::AttachEngine3D
  AttachmentSupport = -> [XY_Plane012]
  MapMode = 5
FEATURE [PartDesign::CoordinateSystem] Local_CS018  label="basement_top_proxy_top_LCS"
  AttacherType = Attacher::AttachEngine3D
  AttachmentOffset = pos=(0,0,3) rot=(0,0,1;0rad)
  AttachmentSupport = -> [XY_Plane012]
  MapMode = 5
  Placement = pos=(0,0,3) rot=(0,0,1;0rad)
FEATURE [PartDesign::Body] Body008  label="basement_top_proxy"
  AllowCompound = false
  Group = -> [Binder006,Pad003,Boolean021,Binder129,Local_CS017,Local_CS018]
  Origin = -> Origin012
  Placement = pos=(0,0,18) rot=(0,0,1;0rad)
  Tip = -> Boolean021
COMPONENT P58 — recipe-attached ("basement_plywood001", modeled in this document).
Construction recipe (the document's own serialized feature program — sketch geometry with constraints, then the solid features built on it; lengths are millimeters unless a unit is written):

FEATURE [PartDesign::SubShapeBinder] Binder005
  BindCopyOnChange = 0
  BindMode = 0
  ClaimChildren = true
  Context = -> Body006 [Binder005.]
  Fuse = false
  MakeFace = true
  OffsetFill = false
  OffsetIntersection = false
  OffsetJoinType = 0
  OffsetOpenResult = false
  PartialLoad = false
  Relative = false
  Support = -> [Array003]
  _Version = 2
FEATURE [PartDesign::Pad] Pad001
  Direction = (0,0,1)
  Length = 18
  Length2 = 10
  Profile = -> Binder005
  Refine = true
  Suppressed = false
  Type = 0
FEATURE [Sketcher::SketchObject] Sketch112
  ArcFitTolerance = 0
  AttachmentSupport = -> [XY_Plane010]
  FullyConstrained = true
  MakeInternals = false
  MapMode = 5
  sketch-geometry (2):
    g0: Circle CenterX=0 CenterY=311.872 CenterZ=0 NormalX=0 NormalY=0 NormalZ=1 AngleXU=0 Radius=2.75
    g1: Circle CenterX=0 CenterY=276.872 CenterZ=0 NormalX=0 NormalY=0 NormalZ=1 AngleXU=0 Radius=2.75
  constraints (6):
    c: PointOnObject(g0,g-2)
    c: PointOnObject(g1,g-2)
    c: Equal(g1,g0)
    c: Diameter(g1) = 5.5
    c: DistanceY(g1,g0) = 35
    c: DistanceY(g1) = 276.872
FEATURE [Sketcher::SketchObject] Sketch113
  ArcFitTolerance = 0
  AttachmentSupport = -> [XY_Plane010]
  FullyConstrained = true
  MakeInternals = false
  MapMode = 5
  sketch-geometry (9):
    g0: LineSegment [constr] StartX=-22.5 StartY=-136 StartZ=0 EndX=-22.5 EndY=-161 EndZ=0
    g1: LineSegment [constr] StartX=-22.5 StartY=-161 StartZ=0 EndX=22.5 EndY=-161 EndZ=0
    g2: LineSegment [constr] StartX=22.5 StartY=-161 StartZ=0 EndX=22.5 EndY=-136 EndZ=0
    g3: LineSegment [constr] StartX=22.5 StartY=-136 StartZ=0 EndX=-22.5 EndY=-136 EndZ=0
    g4: GeomPoint [constr] X=0 Y=-148.5 Z=0
    g5: Circle CenterX=22.5 CenterY=-161 CenterZ=0 NormalX=0 NormalY=0 NormalZ=1 AngleXU=0 Radius=2.75
    g6: Circle CenterX=22.5 CenterY=-136 CenterZ=0 NormalX=0 NormalY=0 NormalZ=1 AngleXU=0 Radius=2.75
    g7: Circle CenterX=-22.5 CenterY=-136 CenterZ=0 NormalX=0 NormalY=0 NormalZ=1 AngleXU=0 Radius=2.75
    g8: Circle CenterX=-22.5 CenterY=-161 CenterZ=0 NormalX=0 NormalY=0 NormalZ=1 AngleXU=0 Radius=2.75
  constraints (21):
    c: Coincident(g0,g1)
    c: Coincident(g1,g2)
    c: Coincident(g2,g3)
    c: Coincident(g3,g0)
    c: Horizontal(g1)
    c: Horizontal(g3)
    c: Vertical(g0)
    c: Vertical(g2)
    c: Symmetric(g1,g0,g4)
    c: PointOnObject(g4,g-2)
    c: Coincident(g5,g1)
    c: Coincident(g6,g2)
    c: Coincident(g7,g0)
    c: Coincident(g8,g0)
    c: Equal(g5,g8)
    c: Equal(g5,g7)
    c: Equal(g5,g6)
    c: Diameter(g5) = 5.5
    c: DistanceY(g2,g2) = 25
    c: DistanceX(g1,g1) = 45
    c: DistanceY(g6) = -136
FEATURE [Sketcher::SketchObject] Sketch166
  ArcFitTolerance = 0
  AttachmentOffset = pos=(349.171,0,0) rot=(0,0,1;0rad)
  AttachmentSupport = -> [YZ_Plane010]
  FullyConstrained = true
  MakeInternals = false
  MapMode = 5
  Placement = pos=(0,349.171,0) rot=(0.57735,0.57735,0.57735;2.0944rad)
  expr: .AttachmentOffset.Base.x = <<basement_sketch>>.Constraints.max_r
  sketch-geometry (3):
    g0: LineSegment StartX=-15 StartY=0 StartZ=0 EndX=0 EndY=15 EndZ=0
    g1: LineSegment StartX=0 StartY=15 StartZ=0 EndX=0 EndY=0 EndZ=0
    g2: LineSegment StartX=0 StartY=0 StartZ=0 EndX=-15 EndY=0 EndZ=0
  constraints (8):
    c: PointOnObject(g0,g-1)
    c: PointOnObject(g0,g-2)
    c: Coincident(g0,g1)
    c: Coincident(g1,g-1)
    c: Coincident(g1,g2)
    c: Coincident(g2,g0)
    c: Equal(g2,g1)
    c: DistanceY(g1,g1) = 15
FEATURE [Sketcher::SketchObject] Sketch216
  ArcFitTolerance = 0
  AttachmentOffset = pos=(350,0,0) rot=(0,0,1;0rad)
  AttachmentSupport = -> [YZ_Plane010]
  FullyConstrained = true
  MakeInternals = false
  MapMode = 5
  Placement = pos=(0,350,0) rot=(0.57735,0.57735,0.57735;2.0944rad)
  sketch-geometry (3):
    g0: LineSegment StartX=0 StartY=15 StartZ=0 EndX=-15 EndY=0 EndZ=0
    g1: LineSegment StartX=-15 StartY=0 StartZ=0 EndX=0 EndY=0 EndZ=0
    g2: LineSegment StartX=0 StartY=15 StartZ=0 EndX=0 EndY=0 EndZ=0
  constraints (8):
    c: PointOnObject(g0,g-2)
    c: PointOnObject(g0,g-1)
    c: Coincident(g0,g1)
    c: Coincident(g1,g-1)
    c: Coincident(g2,g0)
    c: Coincident(g2,g1)
    c: Equal(g1,g2)
    c: DistanceY(g2,g2) = 15
FEATURE [PartDesign::SubtractivePipe] SubtractivePipe
  AuxilleryCurvelinear = true
  AuxillerySpineTangent = false
  BaseFeature = -> Pad001
  Binormal = (0,0,0)
  Mode = 0
  Profile = -> Sketch216
  Spine = -> Binder005 [Edge1,Edge2,Edge3,Edge4,Edge5,Edge6,Edge7,Edge8,Edge9,Edge10,Edge11,Edge12,Edge13,Edge14,Edge15,Edge16,Edge17,Edge18]
  SpineTangent = false
  Suppressed = false
  Transformation = 0
  Transition = 0
FEATURE [PartDesign::Pocket] Pocket062
  BaseFeature = -> SubtractivePipe
  Direction = (0,0,-1)
  Length = 5
  Length2 = 5
  Midplane = true
  Profile = -> Sketch113
  ReferenceAxis = -> Sketch113 [N_Axis]
  Suppressed = false
  Type = 1
FEATURE [PartDesign::CoordinateSystem] Local_CS019  label="basement_top_plywood_bottom_LCS"
  AttacherType = Attacher::AttachEngine3D
  AttachmentSupport = -> [XY_Plane010]
  MapMode = 5
FEATURE [PartDesign::CoordinateSystem] Local_CS020  label="basement_top_plywood_top_LCS"
  AttacherType = Attacher::AttachEngine3D
  AttachmentOffset = pos=(0,0,18) rot=(0,0,1;0rad)
  AttachmentSupport = -> [XY_Plane010]
  MapMode = 5
  Placement = pos=(0,0,18) rot=(0,0,1;0rad)
FEATURE [PartDesign::Boolean] Boolean023
  BaseFeature = -> Pocket062
  Group = -> [Compound066]
  Refine = true
  Suppressed = false
  Type = 1
  UsePlacement = false
FEATURE [PartDesign::Body] Body006  label="basement_top_plywood"
  AllowCompound = false
  Group = -> [Binder005,Pad001,Sketch112,Sketch113,SubtractivePipe,Pocket062,Sketch166,Sketch216,Boolean023,Local_CS019,Local_CS020]
  Origin = -> Origin010
  Tip = -> Boolean023
COMPONENT P59 — recipe-attached ("basement2_amplifier_material_stainlessSteel001", modeled in this document).
Construction recipe (the document's own serialized feature program — sketch geometry with constraints, then the solid features built on it; lengths are millimeters unless a unit is written):

FEATURE [Sketcher::SketchObject] Sketch171  label="basement2_sketch"
  ArcFitTolerance = 0
  AttachmentSupport = -> [XY_Plane080]
  FullyConstrained = true
  MakeInternals = false
  MapMode = 5
  sketch-geometry (10):
    g0: LineSegment StartX=-80 StartY=46.188 StartZ=0 EndX=2.84e-14 EndY=-4.97e-14 EndZ=0
    g1: LineSegment StartX=2.84e-14 StartY=-4.97e-14 StartZ=0 EndX=80 EndY=46.188 EndZ=0
    g2: LineSegment StartX=80 StartY=46.188 StartZ=0 EndX=79.7011 EndY=48.0916 EndZ=0
    g3: LineSegment StartX=79.7011 StartY=48.0916 StartZ=0 EndX=42.5 EndY=285 EndZ=0
    g4: LineSegment StartX=42.5 StartY=285 StartZ=0 EndX=-42.5 EndY=285 EndZ=0
    g5: LineSegment StartX=-42.5 StartY=285 StartZ=0 EndX=-79.7011 EndY=48.0916 EndZ=0
    g6: LineSegment StartX=-79.7011 StartY=48.0916 StartZ=0 EndX=-80 EndY=46.188 EndZ=0
    g7: LineSegment [constr] StartX=80 StartY=46.188 StartZ=0 EndX=81.4991 EndY=44.9774 EndZ=0
    g8: LineSegment [constr] StartX=81.4991 StartY=44.9774 StartZ=0 EndX=84.6406 EndY=48.8672 EndZ=0
    g9: LineSegment [constr] StartX=84.6406 StartY=48.8672 StartZ=0 EndX=79.7011 EndY=48.0916 EndZ=0
  constraints (26):
    c: Coincident(g0,g-1)
    c: Coincident(g0,g1)
    c: Coincident(g1,g2)
    c: Coincident(g2,g3)
    c: Coincident(g3,g4)
    c: Coincident(g4,g5)
    c: Coincident(g5,g6)
    c: Coincident(g6,g0)
    c: Symmetric(g0,g1,g-2)
    c: Symmetric(g4,g3,g-2)
    c: Symmetric(g5,g2,g-2)
    c: Parallel(g2,g3)
    c: Angle(g1) = 0.523599
    c: Coincident(g7,g1)
    c: Symmetric(g7,g2,g1)
    c: DistanceX(g4,g4) = 85
    c: DistanceY(g3) = 285
    c: Coincident(g8,g7)
    c: Coincident(g9,g8)
    c: Coincident(g9,g2)
    c: Perpendicular(g2,g9)
    c: Perpendicular(g7,g8)
    c: Distance(g9) = 5
    c: Distance(g1) = 92.376  'inner_r'
    c: Angle(g7,g2) = 2.40591  'connection_angle'
    c: DistanceX(g0,g1) = 160
FEATURE [PartDesign::FeaturePython] BaseBend044  # WARN: FeaturePython — macro-defined, semantics opaque (R4)
  BendSide = 0
  BendSketch = -> Sketch171
  MidPlane = false
  Reverse = false
  Suppressed = false
  length = 100
  radius = 2
  thickness = 2
FEATURE [PartDesign::FeaturePython] Bend026  # WARN: FeaturePython — macro-defined, semantics opaque (R4)
  AutoMiter = false
  BaseFeature = -> BaseBend044
  BendType = 0
  LengthList = [30]
  LengthSpec = 0
  NonperforationMaxLength = 5
  Perforate = false
  PerforationAngle = 0
  PerforationInitialLength = 5
  PerforationMaxLength = 5
  ReliefFactor = 0.7
  Suppressed = false
  UseReliefFactor = false
  angle = 90
  baseObject = -> BaseBend044 [Edge19,Edge13]
  bendAList = [90]
  extend1 = 0
  extend2 = 0
  gap1 = 0
  gap2 = 0
  invert = false
  kfactor = 0.5
  length = 30
  maxExtendDist = 5
  minGap = 0.1
  minReliefGap = 1
  miterangle1 = 21.0759
  miterangle2 = 21.0759
  offset = 0
  radius = 2
  reliefType = 0
  reliefd = 1
  reliefw = 0.8
  sketchflip = false
  sketchinvert = false
  unfold = false
  expr: miterangle1 = 90 deg - <<basement2_sketch>>.Constraints.connection_angle / 2
  expr: miterangle2 = miterangle1
  expr: radius = BaseBend044.radius
FEATURE [Sketcher::SketchObject] Sketch174
  ArcFitTolerance = 0
  AttachmentSupport = -> [XY_Plane080]
  ExternalGeometry = -> [Sketch171]
  FullyConstrained = true
  MakeInternals = false
  MapMode = 5
  sketch-geometry (7):
    g0: LineSegment StartX=44.3713 StartY=273.083 StartZ=0 EndX=49.3108 EndY=273.858 EndZ=0
    g1: LineSegment StartX=49.3108 StartY=273.858 StartZ=0 EndX=4.93947 EndY=556.429 EndZ=0
    g2: LineSegment StartX=4.93947 StartY=556.429 StartZ=0 EndX=0 EndY=555.654 EndZ=0
    g3: LineSegment StartX=42.5 StartY=285 StartZ=0 EndX=38.2239 EndY=285 EndZ=0
    g4: LineSegment StartX=43.1633 StartY=280.776 StartZ=0 EndX=44.3713 EndY=273.083 EndZ=0
    g5: LineSegment StartX=0 StartY=555.654 StartZ=0 EndX=42.5 EndY=285 EndZ=0
    g6: ArcOfCircle CenterX=38.2239 CenterY=280 CenterZ=0 NormalX=0 NormalY=0 NormalZ=1 AngleXU=0 Radius=5 StartAngle=0.155755 EndAngle=1.5708
  constraints (20):
    c: Coincident(g0,g1)
    c: Coincident(g1,g2)
    c: Coincident(g2,g5)
    c: Coincident(g4,g0)
    c: Parallel(g0,g2)
    c: Perpendicular(g1,g0)
    c: PointOnObject(g0,g-3)
    c: PointOnObject(g2,g-3)
    c: DistanceY(g0) = 273.083
    c: PointOnObject(g2,g-2)
    c: Distance(g0) = 5
    c: Coincident(g3,g-3)
    c: Horizontal(g3)
    c: Parallel(g1,g4)
    c: Parallel(g1,g5)
    c: Coincident(g5,g3)
    c: Tangent(g6,g4) = 1.5708
    c: Tangent(g6,g3) = -1.5708
    c: Radius(g6) = 5
    c: Distance(g3,g0) = 12.0632
FEATURE [PartDesign::Pocket] Pocket105
  BaseFeature = -> Bend026
  Direction = (0,0,-1)
  Length = 5
  Length2 = 5
  Midplane = true
  Profile = -> Sketch174
  ReferenceAxis = -> Sketch174 [N_Axis]
  Suppressed = false
  Type = 1
FEATURE [PartDesign::Mirrored] Mirrored011
  BaseFeature = -> Pocket105
  MirrorPlane = -> Sketch174 [V_Axis]
  Originals = -> [Pocket105]
  Refine = true
  Suppressed = false
  TransformMode = 0
FEATURE [PartDesign::SubShapeBinder] Binder117
  BindCopyOnChange = 0
  BindMode = 0
  ClaimChildren = false
  Context = -> Body107 [Binder117.]
  Fuse = false
  MakeFace = true
  OffsetFill = false
  OffsetIntersection = false
  OffsetJoinType = 0
  OffsetOpenResult = false
  PartialLoad = false
  Relative = true
  Support = -> [Body007[Binder066.Binder064.]]
  _Version = 2
FEATURE [Sketcher::SketchObject] Sketch176
  ArcFitTolerance = 0
  AttachmentSupport = -> [XY_Plane080]
  ExternalGeometry = -> [Sketch171]
  FullyConstrained = true
  MakeInternals = false
  MapMode = 5
  sketch-geometry (5):
    g0: LineSegment StartX=42.5 StartY=285 StartZ=0 EndX=42.5 EndY=362 EndZ=0
    g1: ArcOfCircle CenterX=27.5 CenterY=362 CenterZ=0 NormalX=0 NormalY=0 NormalZ=1 AngleXU=0 Radius=15 StartAngle=-8.4623e-11 EndAngle=1.5708
    g2: LineSegment StartX=0 StartY=285 StartZ=0 EndX=42.5 EndY=285 EndZ=0
    g3: LineSegment StartX=0 StartY=377 StartZ=0 EndX=27.5 EndY=377 EndZ=0
    g4: LineSegment StartX=0 StartY=285 StartZ=0 EndX=0 EndY=377 EndZ=0
  constraints (13):
    c: Coincident(g2,g0)
    c: Vertical(g0)
    c: Coincident(g2,g-3)
    c: Tangent(g0,g1) = -1.5708
    c: PointOnObject(g2,g-2)
    c: PointOnObject(g2,g-3)
    c: PointOnObject(g3,g-2)
    c: Horizontal(g3)
    c: Tangent(g3,g1) = 1.5708
    c: Coincident(g4,g2)
    c: Coincident(g4,g3)
    c: DistanceY(g4,g4) = 92
    c: Radius(g1) = 15
FEATURE [PartDesign::SubShapeBinder] Binder120
  BindCopyOnChange = 0
  BindMode = 0
  ClaimChildren = false
  Context = -> Body107 [Binder120.]
  Fuse = false
  MakeFace = true
  OffsetFill = false
  OffsetIntersection = false
  OffsetJoinType = 0
  OffsetOpenResult = false
  PartialLoad = false
  Relative = true
  Support = -> [Body007[Binder063.]]
  _Version = 2
FEATURE [PartDesign::Pocket] Pocket110
  BaseFeature = -> Mirrored011
  Direction = (0,0,-1)
  Length = 5
  Length2 = 5
  Profile = -> Binder120
  Suppressed = false
  Type = 1
FEATURE [PartDesign::SubShapeBinder] Binder121
  BindCopyOnChange = 0
  BindMode = 0
  ClaimChildren = false
  Context = -> Body107 [Binder121.]
  Fuse = false
  MakeFace = true
  OffsetFill = false
  OffsetIntersection = false
  OffsetJoinType = 0
  OffsetOpenResult = false
  PartialLoad = false
  Relative = true
  Support = -> [Body007[Pocket057.Sketch110.,Pocket058.Sketch111.]]
  _Version = 2
FEATURE [PartDesign::Pocket] Pocket111
  BaseFeature = -> Pocket110
  Direction = (0,0,-1)
  Length = 5
  Length2 = 5
  Midplane = true
  Profile = -> Binder121
  Suppressed = false
  Type = 1
FEATURE [PartDesign::Mirrored] Mirrored012
  BaseFeature = -> Pocket111
  MirrorPlane = -> YZ_Plane080
  Originals = -> [Pocket110]
  Suppressed = false
  TransformMode = 0
FEATURE [PartDesign::FeatureAdditivePython] PDW_Add  # link proxy (typed FeaturePython)
  BaseFeature = -> Mirrored012
  Body = Body107
  ClaimChildren = false
  EditPlacementAdjustments = false
  Enabled = 1
  LinkedObject = -> Mirrored011
  MeshTolerance = 0.1
  PatternBase = -> Mirrored012
  PatternBaseOffset = 0
  PatternBaseScale = 1
  PatternBaseScaleXYZ = (1,1,1)
  PatternOffsetCut = false
  PatternOffsetIntersection = false
  PatternOffsetJoin = 0
  PatternOffsetMode = 0
  PatternOffsetSelfIntersection = false
  PatternOperation = 0
  PatternOperationDefault = None
  PatternScaleCut = false
  PatternShapeOffset = 0
  PatternShapeScale = 1
  PatternShapeScaleXYZ = (1,1,1)
  PatternTool = -> Mirrored011
  PatternToolOffset = 0
  PatternToolScale = 1
  PatternToolScaleXYZ = (1,1,1)
  RefineMesh = true
  ShapeManagement = 0
  ShowMeshProps = false
  ShowOffsetProps = false
  ShowScaleProps = false
  ShowWarnings = true
  Suppressed = false
  TipBase = -> Mirrored012
  TipBaseOffset = 0
  TipBaseScale = 1
  TipBaseScaleXYZ = (1,1,1)
  TipOffsetCut = false
  TipOffsetIntersection = false
  TipOffsetJoin = 0
  TipOffsetMode = 0
  TipOffsetSelfIntersection = false
  TipOperation = 0
  TipOperationDefault = Fuse
  TipScaleCut = false
  TipShapeOffset = 0
  TipShapeScale = 1
  TipShapeScaleXYZ = (1,1,1)
  TipTool = -> Mirrored011
  TipToolOffset = 0
  TipToolScale = 1
  TipToolScaleXYZ = (1,1,1)
  Type = Additive
  UsePatternBaseAddSubShape = false
  UsePatternToolAddSubShape = true
  UseTipBaseAddSubShape = false
  UseTipToolAddSubShape = true
  Version = 0.2023.08.13
FEATURE [PartDesign::FeatureAdditivePython] PDW_Common_Add001  # link proxy (typed FeaturePython)
  BaseFeature = -> PDW_Add
  Body = Body107
  ClaimChildren = false
  EditPlacementAdjustments = false
  Enabled = 1
  LinkedObject = -> Mirrored012
  MeshTolerance = 0.1
  PatternBase = -> PDW_Add
  PatternBaseOffset = 0
  PatternBaseScale = 1
  PatternBaseScaleXYZ = (1,1,1)
  PatternOffsetCut = false
  PatternOffsetIntersection = false
  PatternOffsetJoin = 0
  PatternOffsetMode = 0
  PatternOffsetSelfIntersection = false
  PatternOperation = 3
  PatternOperationDefault = Common
  PatternScaleCut = false
  PatternShapeOffset = 0
  PatternShapeScale = 1
  PatternShapeScaleXYZ = (1,1,1)
  PatternTool = -> Mirrored012
  PatternToolOffset = 0
  PatternToolScale = 1
  PatternToolScaleXYZ = (1,1,1)
  RefineMesh = true
  ShapeManagement = 0
  ShowMeshProps = false
  ShowOffsetProps = false
  ShowScaleProps = false
  ShowWarnings = true
  Suppressed = false
  TipBase = -> PDW_Add
  TipBaseOffset = 0
  TipBaseScale = 1
  TipBaseScaleXYZ = (1,1,1)
  TipOffsetCut = false
  TipOffsetIntersection = false
  TipOffsetJoin = 0
  TipOffsetMode = 0
  TipOffsetSelfIntersection = false
  TipOperation = 2
  TipOperationDefault = Common
  TipScaleCut = false
  TipShapeOffset = 0
  TipShapeScale = 1
  TipShapeScaleXYZ = (1,1,1)
  TipTool = -> Mirrored012
  TipToolOffset = 0
  TipToolScale = 1
  TipToolScaleXYZ = (1,1,1)
  Type = Additive
  UsePatternBaseAddSubShape = false
  UsePatternToolAddSubShape = true
  UseTipBaseAddSubShape = false
  UseTipToolAddSubShape = true
  Version = 0.2023.08.13
FEATURE [PartDesign::PolarPattern] PolarPattern007
  Angle = 360
  Axis = -> Z_Axis080
  BaseFeature = -> PDW_Common_Add001
  Mode = 0
  Occurrences = 3
  Offset = 120
  Originals = -> [PDW_Common_Add001]
  Refine = true
  Suppressed = false
  TransformMode = 0
FEATURE [PartDesign::Pocket] Pocket106
  BaseFeature = -> PolarPattern007
  Direction = (0,0,-1)
  Length = 5
  Length2 = 5
  Midplane = true
  Profile = -> Binder117
  Suppressed = false
  Type = 1
FEATURE [Sketcher::SketchObject] Sketch195
  ArcFitTolerance = 0
  AttachmentSupport = -> [XY_Plane080]
  ExternalGeometry = -> [Sketch174,Sketch171]
  FullyConstrained = true
  MakeInternals = false
  MapMode = 5
  sketch-geometry (9):
    g0: LineSegment StartX=6.08e-14 StartY=555.654 StartZ=0 EndX=42.5 EndY=285 EndZ=0
    g1: LineSegment StartX=42.5 StartY=285 StartZ=0 EndX=0 EndY=285 EndZ=0
    g2: LineSegment StartX=6.08e-14 StartY=555.654 StartZ=0 EndX=0 EndY=555.654 EndZ=0
    g3: LineSegment StartX=0 StartY=555.654 StartZ=0 EndX=0 EndY=285 EndZ=0
    g4: Circle CenterX=36 CenterY=265 CenterZ=0 NormalX=0 NormalY=0 NormalZ=1 AngleXU=0 Radius=2.5
    g5: Circle CenterX=68.9742 CenterY=55.7258 CenterZ=0 NormalX=0 NormalY=0 NormalZ=1 AngleXU=0 Radius=2.5
    g6: Circle CenterX=56.173 CenterY=140.207 CenterZ=0 NormalX=0 NormalY=0 NormalZ=1 AngleXU=0 Radius=2.5
    g7: LineSegment [constr] StartX=68.9742 StartY=55.7258 StartZ=0 EndX=56.173 EndY=140.207 EndZ=0
    g8: LineSegment [constr] StartX=56.173 StartY=140.207 StartZ=0 EndX=36 EndY=265 EndZ=0
  constraints (24):
    c: Coincident(g-3,g0)
    c: Coincident(g0,g-4)
    c: Coincident(g0,g1)
    c: Coincident(g0,g2)
    c: PointOnObject(g2,g-2)
    c: Horizontal(g2)
    c: Coincident(g2,g3)
    c: PointOnObject(g3,g-4)
    c: Vertical(g3)
    c: Coincident(g1,g3)
    c: Diameter(g4) = 5
    c: DistanceX(g-1,g4) = 36
    c: DistanceY(g-1,g4) = 265
    c: Equal(g5,g6)
    c: Equal(g6,g4)
    c: Block(g5)
    c: Block(g6)
    c: Coincident(g7,g5)
    c: Coincident(g7,g6)
    c: Coincident(g8,g6)
    c: Coincident(g8,g4)
    c: DistanceX(g5) = 68.9742
    c: DistanceY(g5) = 55.7258
    c: Distance(g6,g-3) = 419.132
FEATURE [PartDesign::Boolean] Boolean027
  BaseFeature = -> Pocket106
  Group = -> [Populate041,Cylinder012]
  Suppressed = false
  Type = 1
  UsePlacement = false
FEATURE [PartDesign::CoordinateSystem] Local_CS014  label="basement_bottom_amplifier_bottom_LCS"
  AttacherType = Attacher::AttachEngine3D
  AttachmentSupport = -> [XY_Plane080]
  MapMode = 5
FEATURE [PartDesign::CoordinateSystem] Local_CS015  label="basement_bottom_amplifier_top_LCS"
  AttacherType = Attacher::AttachEngine3D
  AttachmentOffset = pos=(0,0,2) rot=(0,0,1;0rad)
  AttachmentSupport = -> [XY_Plane080]
  MapMode = 5
  Placement = pos=(0,0,2) rot=(0,0,1;0rad)
FEATURE [PartDesign::CoordinateSystem] Local_CS048
  AttacherType = Attacher::AttachEngine3D
  AttachmentOffset = pos=(0,0,0) rot=(0,1,0;1.5708rad)
  AttachmentSupport = -> [Sketch171]
  MapMode = 7
  Placement = pos=(42.5,285,0) rot=(0.517473,0.605071,0.605071;2.18654rad)
FEATURE [Sketcher::SketchObject] Sketch272
  ArcFitTolerance = 0
  AttachmentSupport = -> [Local_CS048]
  FullyConstrained = true
  MakeInternals = false
  MapMode = 5
  Placement = pos=(42.5,285,0) rot=(0.517473,0.605071,0.605071;2.18654rad)
FEATURE [PartDesign::Body] Body107  label="basement_bottom_amplifier_material_0.50ansi"
  AllowCompound = false
  Group = -> [Sketch171,BaseBend044,Bend026,Sketch174,Binder117,Pocket105,Sketch176,Binder120,Local_CS048,Sketch272,Mirrored011,Pocket110,Binder121,Pocket111,Sketch195,Mirrored012,PDW_Add,PDW_Common_Add001,PolarPattern007,Pocket106,Boolean027,Local_CS014,Local_CS015]
  Origin = -> Origin080
  Tip = -> Boolean027
COMPONENT P60 — recipe-attached ("basement2_plywood001", modeled in this document).
Construction recipe (the document's own serialized feature program — sketch geometry with constraints, then the solid features built on it; lengths are millimeters unless a unit is written):

FEATURE [PartDesign::SubShapeBinder] Binder003
  BindCopyOnChange = 0
  BindMode = 0
  ClaimChildren = true
  Context = -> Body007 [Binder003.]
  Fuse = false
  MakeFace = true
  OffsetFill = false
  OffsetIntersection = false
  OffsetJoinType = 0
  OffsetOpenResult = false
  PartialLoad = false
  Relative = false
  Support = -> [Array002]
  _Version = 2
FEATURE [PartDesign::Pad] Pad002
  Direction = (0,0,1)
  Length = 18
  Length2 = 10
  Profile = -> Binder003
  Suppressed = false
  Type = 0
FEATURE [Sketcher::SketchObject] Sketch110
  ArcFitTolerance = 0
  AttachmentOffset = pos=(0,333,0) rot=(0,0,1;0rad)
  AttachmentSupport = -> [XY_Plane011]
  FullyConstrained = true
  MakeInternals = false
  MapMode = 5
  Placement = pos=(0,333,0) rot=(0,0,1;0rad)
  sketch-geometry (2):
    g0: Circle CenterX=0 CenterY=26.3 CenterZ=0 NormalX=0 NormalY=0 NormalZ=1 AngleXU=0 Radius=2.75
    g1: Circle CenterX=0 CenterY=-26.3 CenterZ=0 NormalX=0 NormalY=0 NormalZ=1 AngleXU=0 Radius=2.75
  constraints (5):
    c: PointOnObject(g0,g-2)
    c: Equal(g1,g0)
    c: Diameter(g1) = 5.5
    c: Symmetric(g1,g0,g-1)
    c: DistanceY(g1,g0) = 52.6
FEATURE [PartDesign::PolarPattern] PolarPattern002
  Angle = 360
  Axis = -> Z_Axis011
  BaseFeature = -> Pad002
  Mode = 0
  Occurrences = 3
  Offset = 120
  Suppressed = false
  TransformMode = 0
FEATURE [Sketcher::SketchObject] Sketch178
  ArcFitTolerance = 0
  AttachmentSupport = -> [XY_Plane011]
  FullyConstrained = true
  MakeInternals = false
  MapMode = 5
  sketch-geometry (4):
    g0: Circle CenterX=29 CenterY=-145.633 CenterZ=0 NormalX=0 NormalY=0 NormalZ=1 AngleXU=0 Radius=4.25
    g1: LineSegment [constr] StartX=0 StartY=0 StartZ=0 EndX=84.8108 EndY=-48.9655 EndZ=0
    g2: Circle CenterX=140.622 CenterY=47.7016 CenterZ=0 NormalX=0 NormalY=0 NormalZ=1 AngleXU=0 Radius=4.25
    g3: LineSegment [constr] StartX=140.622 StartY=47.7016 StartZ=0 EndX=29 EndY=-145.633 EndZ=0
  constraints (10):
    c: Diameter(g0) = 8.5
    c: DistanceX(g0) = 29
    c: DistanceY(g0) = -145.633
    c: Coincident(g1,g-1)
    c: Angle(g1) = -0.523599
    c: Symmetric(g2,g0,g1)
    c: Equal(g2,g0)
    c: Coincident(g3,g2)
    c: Coincident(g3,g0)
    c: PointOnObject(g1,g3)
FEATURE [Sketcher::SketchObject] Sketch218
  ArcFitTolerance = 0
  AttachmentOffset = pos=(0,0,18) rot=(0,0,1;0rad)
  AttachmentSupport = -> [XY_Plane011]
  FullyConstrained = false
  MakeInternals = false
  MapMode = 5
  Placement = pos=(0,0,18) rot=(0,0,1;0rad)
  sketch-geometry (4):
    g0: LineSegment StartX=93.4507 StartY=-44.023 StartZ=0 EndX=107.489 EndY=-44.023 EndZ=0
    g1: LineSegment StartX=107.489 StartY=-44.023 StartZ=0 EndX=107.489 EndY=-29.1068 EndZ=0
    g2: LineSegment StartX=107.489 StartY=-29.1068 StartZ=0 EndX=93.4507 EndY=-29.1068 EndZ=0
    g3: LineSegment StartX=93.4507 StartY=-29.1068 StartZ=0 EndX=93.4507 EndY=-44.023 EndZ=0
  constraints (8):
    c: Coincident(g0,g1)
    c: Coincident(g1,g2)
    c: Coincident(g2,g3)
    c: Coincident(g3,g0)
    c: Horizontal(g0)
    c: Horizontal(g2)
    c: Vertical(g1)
    c: Vertical(g3)
FEATURE [PartDesign::Boolean] Boolean026
  BaseFeature = -> Pad002
  Group = -> [Compound069]
  Suppressed = false
  Type = 1
  UsePlacement = false
FEATURE [PartDesign::CoordinateSystem] Local_CS010  label="basement_bottom_plywood_bottom"
  AttacherType = Attacher::AttachEngine3D
  AttachmentSupport = -> [XY_Plane011]
  MapMode = 5
FEATURE [PartDesign::CoordinateSystem] Local_CS011  label="basement_bottom_plywood_top"
  AttacherType = Attacher::AttachEngine3D
  AttachmentOffset = pos=(0,0,18) rot=(0,0,1;0rad)
  AttachmentSupport = -> [XY_Plane011]
  MapMode = 5
  Placement = pos=(0,0,18) rot=(0,0,1;0rad)
FEATURE [PartDesign::Body] Body007  label="basement_bottom_plywood"
  AllowCompound = false
  Group = -> [Binder003,Pad002,Sketch110,PolarPattern002,Sketch178,Boolean026,Sketch218,Local_CS010,Local_CS011]
  Origin = -> Origin011
  Tip = -> Boolean026
